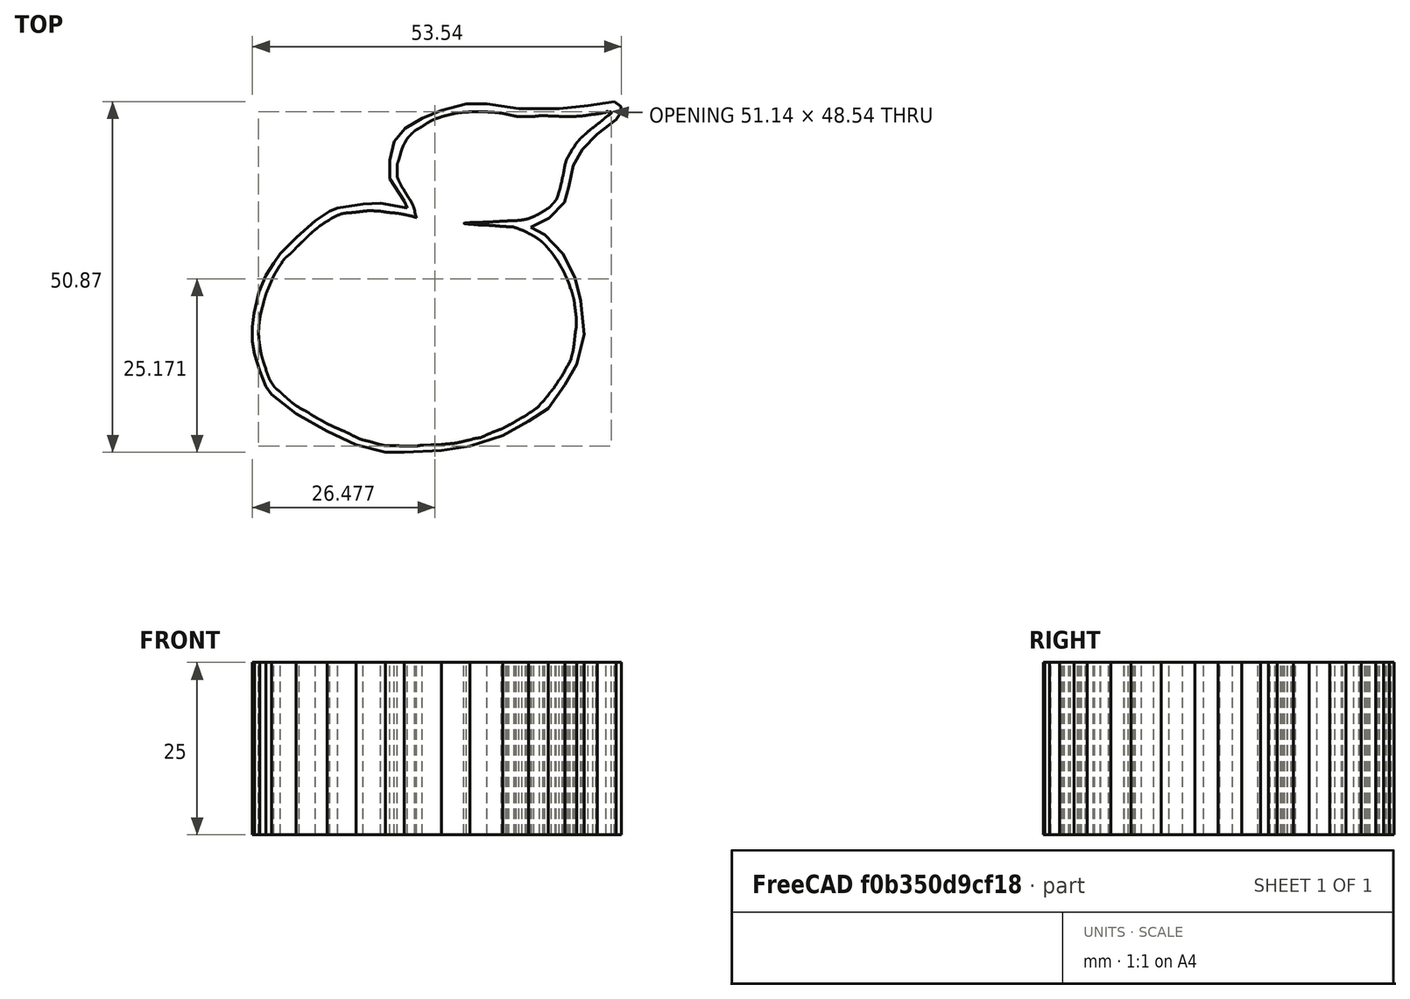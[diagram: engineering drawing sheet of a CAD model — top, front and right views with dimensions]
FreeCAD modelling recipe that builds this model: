
FCSTD DOCUMENT  (FreeCAD 0.18.3R)
Label: apple2
License: All rights reserved
LicenseURL: http://en.wikipedia.org/wiki/All_rights_reserved
objects: Part::Part2DObjectPython×3, Sketcher::SketchObject×2, Part::Extrusion×2, Part::Cut×1
note: 8 computed .brp shape members not serialized (recipe doc carries the construction recipe); baked Part::Feature solids carry a one-line shape summary decoded from their .brp

FEATURE [Sketcher::SketchObject] Sketch1180
  sketch-geometry (1180):
    g0: ArcOfCircle CenterX=919.407 CenterY=1602.46 CenterZ=0 NormalX=0 NormalY=0 NormalZ=1 AngleXU=-3.14159 Radius=144.686 StartAngle=1.63984 EndAngle=1.65794
    g1: ArcOfCircle CenterX=768.629 CenterY=1404.83 CenterZ=0 NormalX=0 NormalY=0 NormalZ=1 AngleXU=-3.14159 Radius=0.829803 StartAngle=1.5708 EndAngle=2.04218
    g2: ArcOfCircle CenterX=851.715 CenterY=737.772 CenterZ=0 NormalX=0 NormalY=0 NormalZ=1 AngleXU=0 Radius=243.363 StartAngle=4.83011 EndAngle=4.84867
    g3: ArcOfCircle CenterX=879.744 CenterY=533.379 CenterZ=0 NormalX=0 NormalY=0 NormalZ=1 AngleXU=0 Radius=37.0576 StartAngle=4.84867 EndAngle=4.92323
    g4: ArcOfCircle CenterX=1330.58 CenterY=-1573.07 CenterZ=0 NormalX=0 NormalY=0 NormalZ=1 AngleXU=-3.14159 Radius=2117.1 StartAngle=4.9221 EndAngle=4.92323
    g5: ArcOfCircle CenterX=1556.93 CenterY=-2624.68 CenterZ=0 NormalX=0 NormalY=0 NormalZ=1 AngleXU=-3.14159 Radius=3192.79 StartAngle=4.9201 EndAngle=4.92096
    g6: ArcOfCircle CenterX=2022.48 CenterY=-4824.32 CenterZ=0 NormalX=0 NormalY=0 NormalZ=1 AngleXU=-3.14159 Radius=5441.15 StartAngle=4.92096 EndAngle=4.92153
    g7: ArcOfCircle CenterX=874.349 CenterY=614.069 CenterZ=0 NormalX=0 NormalY=0 NormalZ=1 AngleXU=0 Radius=117.109 StartAngle=4.9201 EndAngle=4.944
    g8: ArcOfCircle CenterX=845.401 CenterY=736.81 CenterZ=0 NormalX=0 NormalY=0 NormalZ=1 AngleXU=0 Radius=243.218 StartAngle=4.944 EndAngle=4.95783
    g9: ArcOfCircle CenterX=845.173 CenterY=737.72 CenterZ=0 NormalX=0 NormalY=0 NormalZ=1 AngleXU=0 Radius=244.155 StartAngle=4.95783 EndAngle=4.97166
    g10: ArcOfCircle CenterX=1979.85 CenterY=-4623.55 CenterZ=0 NormalX=0 NormalY=0 NormalZ=1 AngleXU=-3.14159 Radius=5235.91 StartAngle=4.92153 EndAngle=4.9221
    g11: ArcOfCircle CenterX=876.443 CenterY=619.827 CenterZ=0 NormalX=0 NormalY=0 NormalZ=1 AngleXU=0 Radius=122.186 StartAngle=4.97166 EndAngle=4.99486
    g12: ArcOfCircle CenterX=928.112 CenterY=441.8 CenterZ=0 NormalX=0 NormalY=0 NormalZ=1 AngleXU=-3.14159 Radius=63.1874 StartAngle=4.95011 EndAngle=4.99486
    g13: ArcOfCircle CenterX=942.49 CenterY=382.464 CenterZ=0 NormalX=0 NormalY=0 NormalZ=1 AngleXU=-3.14159 Radius=124.24 StartAngle=4.92313 EndAngle=4.95011
    g14: ArcOfCircle CenterX=942.314 CenterY=383.285 CenterZ=0 NormalX=0 NormalY=0 NormalZ=1 AngleXU=-3.14159 Radius=123.4 StartAngle=4.89612 EndAngle=4.92313
    g15: ArcOfCircle CenterX=-1401.43 CenterY=-23166.9 CenterZ=0 NormalX=0 NormalY=0 NormalZ=1 AngleXU=0 Radius=24413 StartAngle=1.472 EndAngle=1.47223
    g16: ArcOfCircle CenterX=959.527 CenterY=1204.98 CenterZ=0 NormalX=0 NormalY=0 NormalZ=1 AngleXU=-3.14159 Radius=75.4491 StartAngle=1.45086 EndAngle=1.50424
    g17: ArcOfCircle CenterX=835.893 CenterY=1420.5 CenterZ=0 NormalX=0 NormalY=0 NormalZ=1 AngleXU=0 Radius=19.2721 StartAngle=1.8395 EndAngle=1.92574
    g18: ArcOfCircle CenterX=817.137 CenterY=1499.08 CenterZ=0 NormalX=0 NormalY=0 NormalZ=1 AngleXU=-3.14159 Radius=61.6309 StartAngle=1.89221 EndAngle=1.9355
    g19: ArcOfCircle CenterX=818.555 CenterY=1494.83 CenterZ=0 NormalX=0 NormalY=0 NormalZ=1 AngleXU=-3.14159 Radius=57.1444 StartAngle=1.84833 EndAngle=1.89221
    g20: ArcOfCircle CenterX=829.435 CenterY=1434.63 CenterZ=0 NormalX=0 NormalY=0 NormalZ=1 AngleXU=0 Radius=3.72542 StartAngle=2.01413 EndAngle=2.28314
    g21: ArcOfCircle CenterX=-7440.76 CenterY=-3669.64 CenterZ=0 NormalX=0 NormalY=0 NormalZ=1 AngleXU=-3.14159 Radius=9532.58 StartAngle=3.67931 EndAngle=3.67962
    g22: ArcOfCircle CenterX=768.629 CenterY=1402.13 CenterZ=0 NormalX=0 NormalY=0 NormalZ=1 AngleXU=0 Radius=1.86919 StartAngle=1.5708 EndAngle=2.30518
    g23: ArcOfCircle CenterX=1058.34 CenterY=669.531 CenterZ=0 NormalX=0 NormalY=0 NormalZ=1 AngleXU=0 Radius=803.247 StartAngle=1.81901 EndAngle=1.83669
    g24: ArcOfCircle CenterX=902.501 CenterY=1384.26 CenterZ=0 NormalX=0 NormalY=0 NormalZ=1 AngleXU=0 Radius=71.5381 StartAngle=1.69996 EndAngle=1.76066
    g25: ArcOfCircle CenterX=1318.79 CenterY=1567.21 CenterZ=0 NormalX=0 NormalY=0 NormalZ=1 AngleXU=0 Radius=673.017 StartAngle=3.67003 EndAngle=3.67544
    g26: ArcOfCircle CenterX=818.017 CenterY=3068.57 CenterZ=0 NormalX=0 NormalY=0 NormalZ=1 AngleXU=-3.14159 Radius=1614.3 StartAngle=1.63675 EndAngle=1.63984
    g27: ArcOfCircle CenterX=960.92 CenterY=1080.29 CenterZ=0 NormalX=0 NormalY=0 NormalZ=1 AngleXU=0 Radius=381.072 StartAngle=1.76067 EndAngle=1.79575
    g28: ArcOfCircle CenterX=786.319 CenterY=1347.74 CenterZ=0 NormalX=0 NormalY=0 NormalZ=1 AngleXU=0 Radius=52.1702 StartAngle=2.6013 EndAngle=2.67939
    g29: ArcOfCircle CenterX=2179.89 CenterY=0.0273162 CenterZ=0 NormalX=0 NormalY=0 NormalZ=1 AngleXU=0 Radius=1991.54 StartAngle=2.36577 EndAngle=2.37248
    g30: ArcOfCircle CenterX=857.853 CenterY=1405.69 CenterZ=0 NormalX=0 NormalY=0 NormalZ=1 AngleXU=0 Radius=40.2748 StartAngle=1.83669 EndAngle=1.99252
    g31: ArcOfCircle CenterX=791.991 CenterY=1412.51 CenterZ=0 NormalX=0 NormalY=0 NormalZ=1 AngleXU=0 Radius=4.93289 StartAngle=2.04902 EndAngle=2.19191
    g32: ArcOfCircle CenterX=923.045 CenterY=1227.68 CenterZ=0 NormalX=0 NormalY=0 NormalZ=1 AngleXU=0 Radius=231.243 StartAngle=2.07905 EndAngle=2.11989
    g33: ArcOfCircle CenterX=790.165 CenterY=1416.03 CenterZ=0 NormalX=0 NormalY=0 NormalZ=1 AngleXU=0 Radius=0.966328 StartAngle=1.5708 EndAngle=2.04902
    g34: ArcOfCircle CenterX=849.435 CenterY=1309.77 CenterZ=0 NormalX=0 NormalY=0 NormalZ=1 AngleXU=0 Radius=125.829 StartAngle=2.52191 EndAngle=2.56028
    g35: ArcOfCircle CenterX=790.165 CenterY=1418.14 CenterZ=0 NormalX=0 NormalY=0 NormalZ=1 AngleXU=-3.14159 Radius=1.13895 StartAngle=1.5708 EndAngle=2.10185
    g36: ArcOfCircle CenterX=790.392 CenterY=1278.24 CenterZ=0 NormalX=0 NormalY=0 NormalZ=1 AngleXU=0 Radius=74.222 StartAngle=3.20651 EndAngle=3.26556
    g37: ArcOfCircle CenterX=-7666.65 CenterY=-3804.43 CenterZ=0 NormalX=0 NormalY=0 NormalZ=1 AngleXU=-3.14159 Radius=9795.63 StartAngle=3.67962 EndAngle=3.67998
    g38: ArcOfCircle CenterX=826.334 CenterY=1314.34 CenterZ=0 NormalX=0 NormalY=0 NormalZ=1 AngleXU=0 Radius=106.8 StartAngle=2.02372 EndAngle=2.05292
    g39: ArcOfCircle CenterX=729.391 CenterY=1270.64 CenterZ=0 NormalX=0 NormalY=0 NormalZ=1 AngleXU=0 Radius=12.7493 StartAngle=3.26556 EndAngle=3.48294
    g40: ArcOfCircle CenterX=758.719 CenterY=1471.68 CenterZ=0 NormalX=0 NormalY=0 NormalZ=1 AngleXU=-3.14159 Radius=63.2306 StartAngle=2.10185 EndAngle=2.13158
    g41: ArcOfCircle CenterX=845.323 CenterY=1281.82 CenterZ=0 NormalX=0 NormalY=0 NormalZ=1 AngleXU=0 Radius=129.27 StartAngle=3.16027 EndAngle=3.20651
    g42: ArcOfCircle CenterX=1491.75 CenterY=1626.11 CenterZ=0 NormalX=0 NormalY=0 NormalZ=1 AngleXU=0 Radius=854.254 StartAngle=3.59782 EndAngle=3.61137
    g43: ArcOfCircle CenterX=1175.24 CenterY=1470.78 CenterZ=0 NormalX=0 NormalY=0 NormalZ=1 AngleXU=0 Radius=501.69 StartAngle=3.5752 EndAngle=3.59782
    g44: ArcOfCircle CenterX=785.625 CenterY=1259.2 CenterZ=0 NormalX=0 NormalY=0 NormalZ=1 AngleXU=0 Radius=57.2786 StartAngle=3.6364 EndAngle=3.66505
    g45: ArcOfCircle CenterX=746.533 CenterY=1478.31 CenterZ=0 NormalX=0 NormalY=0 NormalZ=1 AngleXU=-3.14159 Radius=75.56 StartAngle=2.02372 EndAngle=2.06479
    g46: ArcOfCircle CenterX=490.211 CenterY=1496.45 CenterZ=0 NormalX=0 NormalY=0 NormalZ=1 AngleXU=-3.14159 Radius=279.168 StartAngle=2.64115 EndAngle=2.64999
    g47: ArcOfCircle CenterX=753.834 CenterY=1464.76 CenterZ=0 NormalX=0 NormalY=0 NormalZ=1 AngleXU=-3.14159 Radius=60.1638 StartAngle=2.06479 EndAngle=2.11351
    g48: ArcOfCircle CenterX=847.491 CenterY=1311.04 CenterZ=0 NormalX=0 NormalY=0 NormalZ=1 AngleXU=0 Radius=123.503 StartAngle=2.56029 EndAngle=2.6013
    g49: ArcOfCircle CenterX=394.968 CenterY=1424.23 CenterZ=0 NormalX=0 NormalY=0 NormalZ=1 AngleXU=-3.14159 Radius=342.253 StartAngle=2.85482 EndAngle=2.86963
    g50: ArcOfCircle CenterX=787.781 CenterY=1291.39 CenterZ=0 NormalX=0 NormalY=0 NormalZ=1 AngleXU=0 Radius=74.7144 StartAngle=3.48294 EndAngle=3.5752
    g51: ArcOfCircle CenterX=814.71 CenterY=1336.09 CenterZ=0 NormalX=0 NormalY=0 NormalZ=1 AngleXU=0 Radius=82.1386 StartAngle=2.08653 EndAngle=2.11719
    g52: ArcOfCircle CenterX=756.113 CenterY=1460.98 CenterZ=0 NormalX=0 NormalY=0 NormalZ=1 AngleXU=-3.14159 Radius=55.7495 StartAngle=2.11351 EndAngle=2.15768
    g53: ArcOfCircle CenterX=945.228 CenterY=1187.86 CenterZ=0 NormalX=0 NormalY=0 NormalZ=1 AngleXU=0 Radius=276.826 StartAngle=2.04638 EndAngle=2.07905
    g54: LineSegment StartX=719.98 StartY=1316.94 StartZ=0 EndX=716 EndY=1304.86 EndZ=0
    g55: ArcOfCircle CenterX=1275.84 CenterY=1542.14 CenterZ=0 NormalX=0 NormalY=0 NormalZ=1 AngleXU=0 Radius=623.287 StartAngle=3.66505 EndAngle=3.67003
    g56: ArcOfCircle CenterX=884.535 CenterY=1273.75 CenterZ=0 NormalX=0 NormalY=0 NormalZ=1 AngleXU=0 Radius=174.829 StartAngle=2.30518 EndAngle=2.33402
    g57: ArcOfCircle CenterX=748.085 CenterY=1486.13 CenterZ=0 NormalX=0 NormalY=0 NormalZ=1 AngleXU=-3.14159 Radius=81.1549 StartAngle=2.17574 EndAngle=2.20706
    g58: ArcOfCircle CenterX=706.781 CenterY=1215.33 CenterZ=0 NormalX=0 NormalY=0 NormalZ=1 AngleXU=-3.14159 Radius=32.9861 StartAngle=3.71073 EndAngle=3.75642
    g59: ArcOfCircle CenterX=357.829 CenterY=1435.18 CenterZ=0 NormalX=0 NormalY=0 NormalZ=1 AngleXU=-3.14159 Radius=380.974 StartAngle=2.84009 EndAngle=2.85482
    g60: ArcOfCircle CenterX=765.534 CenterY=1410.9 CenterZ=0 NormalX=0 NormalY=0 NormalZ=1 AngleXU=-3.14159 Radius=7.64444 StartAngle=2.04218 EndAngle=2.13431
    g61: ArcOfCircle CenterX=764.784 CenterY=1412.09 CenterZ=0 NormalX=0 NormalY=0 NormalZ=1 AngleXU=-3.14159 Radius=9.04854 StartAngle=2.13431 EndAngle=2.22753
    g62: ArcOfCircle CenterX=648.737 CenterY=1353.46 CenterZ=0 NormalX=0 NormalY=0 NormalZ=1 AngleXU=-3.14159 Radius=78.8009 StartAngle=2.86963 EndAngle=2.91371
    g63: ArcOfCircle CenterX=720.624 CenterY=1226.06 CenterZ=0 NormalX=0 NormalY=0 NormalZ=1 AngleXU=-3.14159 Radius=15.4663 StartAngle=3.80221 EndAngle=3.88226
    g64: ArcOfCircle CenterX=826.535 CenterY=1418.33 CenterZ=0 NormalX=0 NormalY=0 NormalZ=1 AngleXU=0 Radius=17.5895 StartAngle=1.80228 EndAngle=2.04638
    g65: ArcOfCircle CenterX=416.988 CenterY=1416.79 CenterZ=0 NormalX=0 NormalY=0 NormalZ=1 AngleXU=-3.14159 Radius=319.02 StartAngle=2.82326 EndAngle=2.84009
    g66: LineSegment StartX=716 StartY=1304.86 StartZ=0 EndX=716 EndY=1287.56 EndZ=0
    g67: ArcOfCircle CenterX=632.711 CenterY=1424.26 CenterZ=0 NormalX=0 NormalY=0 NormalZ=1 AngleXU=-3.14159 Radius=119.445 StartAngle=2.6635 EndAngle=2.67939
    g68: ArcOfCircle CenterX=763.283 CenterY=1371.23 CenterZ=0 NormalX=0 NormalY=0 NormalZ=1 AngleXU=0 Radius=19.9993 StartAngle=2.37248 EndAngle=2.52191
    g69: ArcOfCircle CenterX=784.642 CenterY=1418.08 CenterZ=0 NormalX=0 NormalY=0 NormalZ=1 AngleXU=-3.14159 Radius=4.23293 StartAngle=2.15768 EndAngle=2.44887
    g70: ArcOfCircle CenterX=831.516 CenterY=1311.07 CenterZ=0 NormalX=0 NormalY=0 NormalZ=1 AngleXU=0 Radius=108.829 StartAngle=2.84728 EndAngle=2.91371
    g71: ArcOfCircle CenterX=720.065 CenterY=1223.83 CenterZ=0 NormalX=0 NormalY=0 NormalZ=1 AngleXU=-3.14159 Radius=17.2153 StartAngle=3.63639 EndAngle=3.71073
    g72: ArcOfCircle CenterX=817.882 CenterY=1330.49 CenterZ=0 NormalX=0 NormalY=0 NormalZ=1 AngleXU=0 Radius=88.57 StartAngle=2.05293 EndAngle=2.08652
    g73: ArcOfCircle CenterX=793.243 CenterY=1410.94 CenterZ=0 NormalX=0 NormalY=0 NormalZ=1 AngleXU=0 Radius=6.94498 StartAngle=2.3262 EndAngle=2.44887
    g74: ArcOfCircle CenterX=741.67 CenterY=1245.31 CenterZ=0 NormalX=0 NormalY=0 NormalZ=1 AngleXU=0 Radius=13.0499 StartAngle=3.61137 EndAngle=3.88226
    g75: ArcOfCircle CenterX=707.064 CenterY=1215.53 CenterZ=0 NormalX=0 NormalY=0 NormalZ=1 AngleXU=-3.14159 Radius=32.6394 StartAngle=3.75641 EndAngle=3.8022
    g76: ArcOfCircle CenterX=818.993 CenterY=1449.96 CenterZ=0 NormalX=0 NormalY=0 NormalZ=1 AngleXU=-3.14159 Radius=14.9207 StartAngle=1.98949 EndAngle=2.07606
    g77: ArcOfCircle CenterX=763.401 CenterY=1413.88 CenterZ=0 NormalX=0 NormalY=0 NormalZ=1 AngleXU=-3.14159 Radius=11.3144 StartAngle=2.22753 EndAngle=2.30636
    g78: ArcOfCircle CenterX=785.154 CenterY=1335.15 CenterZ=0 NormalX=0 NormalY=0 NormalZ=1 AngleXU=0 Radius=56.9989 StartAngle=2.64115 EndAngle=2.7451
    g79: ArcOfCircle CenterX=381.455 CenterY=1554.68 CenterZ=0 NormalX=0 NormalY=0 NormalZ=1 AngleXU=-3.14159 Radius=402.533 StartAngle=2.64999 EndAngle=2.65671
    g80: ArcOfCircle CenterX=1152.7 CenterY=1287.56 CenterZ=0 NormalX=0 NormalY=0 NormalZ=1 AngleXU=0 Radius=436.695 StartAngle=3.14159 EndAngle=3.16027
    g81: ArcOfCircle CenterX=765.072 CenterY=1461.56 CenterZ=0 NormalX=0 NormalY=0 NormalZ=1 AngleXU=-3.14159 Radius=51.287 StartAngle=2.13158 EndAngle=2.17574
    g82: ArcOfCircle CenterX=877.006 CenterY=1297.28 CenterZ=0 NormalX=0 NormalY=0 NormalZ=1 AngleXU=0 Radius=156.362 StartAngle=2.79665 EndAngle=2.84728
    g83: ArcOfCircle CenterX=231.475 CenterY=905.528 CenterZ=0 NormalX=0 NormalY=0 NormalZ=1 AngleXU=-3.14159 Radius=599.756 StartAngle=3.67696 EndAngle=3.67931
    g84: ArcOfCircle CenterX=792.702 CenterY=1411.52 CenterZ=0 NormalX=0 NormalY=0 NormalZ=1 AngleXU=0 Radius=6.15492 StartAngle=2.19191 EndAngle=2.3262
    g85: ArcOfCircle CenterX=775.589 CenterY=1400.42 CenterZ=0 NormalX=0 NormalY=0 NormalZ=1 AngleXU=0 Radius=6.84968 StartAngle=2.11719 EndAngle=2.30636
    g86: ArcOfCircle CenterX=867.091 CenterY=1300.85 CenterZ=0 NormalX=0 NormalY=0 NormalZ=1 AngleXU=0 Radius=145.827 StartAngle=2.7451 EndAngle=2.79665
    g87: ArcOfCircle CenterX=772.459 CenterY=1226.42 CenterZ=0 NormalX=0 NormalY=0 NormalZ=1 AngleXU=0 Radius=29.2364 StartAngle=3.67696 EndAngle=3.7198
    g88: ArcOfCircle CenterX=835.53 CenterY=1421.82 CenterZ=0 NormalX=0 NormalY=0 NormalZ=1 AngleXU=0 Radius=17.9038 StartAngle=1.74836 EndAngle=1.8395
    g89: ArcOfCircle CenterX=904.424 CenterY=1312.54 CenterZ=0 NormalX=0 NormalY=0 NormalZ=1 AngleXU=0 Radius=186.816 StartAngle=3.7198 EndAngle=3.73068
    g90: ArcOfCircle CenterX=809.835 CenterY=3192.41 CenterZ=0 NormalX=0 NormalY=0 NormalZ=1 AngleXU=-3.14159 Radius=1738.4 StartAngle=1.63339 EndAngle=1.63676
    g91: ArcOfCircle CenterX=932.6 CenterY=1147.45 CenterZ=0 NormalX=0 NormalY=0 NormalZ=1 AngleXU=0 Radius=310.256 StartAngle=1.6562 EndAngle=1.67798
    g92: ArcOfCircle CenterX=927.225 CenterY=1210.23 CenterZ=0 NormalX=0 NormalY=0 NormalZ=1 AngleXU=0 Radius=247.251 StartAngle=1.63039 EndAngle=1.6562
    g93: ArcOfCircle CenterX=923.157 CenterY=1325.06 CenterZ=0 NormalX=0 NormalY=0 NormalZ=1 AngleXU=0 Radius=209.348 StartAngle=3.73068 EndAngle=3.74177
    g94: ArcOfCircle CenterX=846.043 CenterY=1353.53 CenterZ=0 NormalX=0 NormalY=0 NormalZ=1 AngleXU=0 Radius=83.7041 StartAngle=2.11989 EndAngle=2.20705
    g95: ArcOfCircle CenterX=1410.52 CenterY=1621.43 CenterZ=0 NormalX=0 NormalY=0 NormalZ=1 AngleXU=0 Radius=779.574 StartAngle=3.67544 EndAngle=3.68028
    g96: ArcOfCircle CenterX=638.353 CenterY=1133.6 CenterZ=0 NormalX=0 NormalY=0 NormalZ=1 AngleXU=-3.14159 Radius=134.188 StartAngle=3.53735 EndAngle=3.62538
    g97: ArcOfCircle CenterX=920.69 CenterY=1323.37 CenterZ=0 NormalX=0 NormalY=0 NormalZ=1 AngleXU=0 Radius=206.358 StartAngle=3.74177 EndAngle=3.75298
    g98: ArcOfCircle CenterX=684.77 CenterY=1157.99 CenterZ=0 NormalX=0 NormalY=0 NormalZ=1 AngleXU=-3.14159 Radius=81.7539 StartAngle=3.62538 EndAngle=3.75298
    g99: ArcOfCircle CenterX=1023.04 CenterY=808.811 CenterZ=0 NormalX=0 NormalY=0 NormalZ=1 AngleXU=0 Radius=659.564 StartAngle=1.79575 EndAngle=1.81901
    g100: ArcOfCircle CenterX=930.36 CenterY=1225.85 CenterZ=0 NormalX=0 NormalY=0 NormalZ=1 AngleXU=0 Radius=241.122 StartAngle=2.33402 EndAngle=2.36577
    g101: ArcOfCircle CenterX=527.147 CenterY=1081.42 CenterZ=0 NormalX=0 NormalY=0 NormalZ=1 AngleXU=0 Radius=57.8297 StartAngle=2.2214 EndAngle=2.2808
    g102: ArcOfCircle CenterX=819.57 CenterY=1447.88 CenterZ=0 NormalX=0 NormalY=0 NormalZ=1 AngleXU=-3.14159 Radius=12.7698 StartAngle=1.80228 EndAngle=1.90496
    g103: ArcOfCircle CenterX=744.818 CenterY=1168.33 CenterZ=0 NormalX=0 NormalY=0 NormalZ=1 AngleXU=-3.14159 Radius=22.1823 StartAngle=3.14159 EndAngle=3.45253
    g104: ArcOfCircle CenterX=643.698 CenterY=1135.83 CenterZ=0 NormalX=0 NormalY=0 NormalZ=1 AngleXU=-3.14159 Radius=128.395 StartAngle=3.45253 EndAngle=3.53735
    g105: ArcOfCircle CenterX=407.079 CenterY=1541.18 CenterZ=0 NormalX=0 NormalY=0 NormalZ=1 AngleXU=-3.14159 Radius=373.57 StartAngle=2.65671 EndAngle=2.6635
    g106: ArcOfCircle CenterX=929.419 CenterY=1177.02 CenterZ=0 NormalX=0 NormalY=0 NormalZ=1 AngleXU=0 Radius=280.516 StartAngle=1.67798 EndAngle=1.69996
    g107: ArcOfCircle CenterX=791.717 CenterY=3481.48 CenterZ=0 NormalX=0 NormalY=0 NormalZ=1 AngleXU=-3.14159 Radius=2028.05 StartAngle=1.63039 EndAngle=1.63339
    g108: ArcOfCircle CenterX=829.023 CenterY=1458.08 CenterZ=0 NormalX=0 NormalY=0 NormalZ=1 AngleXU=-3.14159 Radius=18.9368 StartAngle=1.74836 EndAngle=1.84833
    g109: ArcOfCircle CenterX=818.33 CenterY=1451.45 CenterZ=0 NormalX=0 NormalY=0 NormalZ=1 AngleXU=-3.14159 Radius=16.5511 StartAngle=1.90496 EndAngle=1.9895
    g110: ArcOfCircle CenterX=823.892 CenterY=1481.39 CenterZ=0 NormalX=0 NormalY=0 NormalZ=1 AngleXU=-3.14159 Radius=42.6938 StartAngle=1.9355 EndAngle=1.99252
    g111: ArcOfCircle CenterX=834.995 CenterY=1422.92 CenterZ=0 NormalX=0 NormalY=0 NormalZ=1 AngleXU=0 Radius=16.6868 StartAngle=1.92574 EndAngle=2.01413
    g112: ArcOfCircle CenterX=823.975 CenterY=1440.95 CenterZ=0 NormalX=0 NormalY=0 NormalZ=1 AngleXU=-3.14159 Radius=4.62783 StartAngle=2.07606 EndAngle=2.28314
    g113: ArcOfCircle CenterX=-9815.61 CenterY=-5087.87 CenterZ=0 NormalX=0 NormalY=0 NormalZ=1 AngleXU=-3.14159 Radius=12298.7 StartAngle=3.67998 EndAngle=3.68028
    g114: ArcOfCircle CenterX=773.371 CenterY=1168.33 CenterZ=0 NormalX=0 NormalY=0 NormalZ=1 AngleXU=0 Radius=6.37126 StartAngle=3.14159 EndAngle=3.34669
    g115: ArcOfCircle CenterX=840.588 CenterY=1182.31 CenterZ=0 NormalX=0 NormalY=0 NormalZ=1 AngleXU=0 Radius=75.027 StartAngle=3.34669 EndAngle=3.38037
    g116: ArcOfCircle CenterX=846.631 CenterY=1183.78 CenterZ=0 NormalX=0 NormalY=0 NormalZ=1 AngleXU=0 Radius=81.2468 StartAngle=3.38037 EndAngle=3.41711
    g117: ArcOfCircle CenterX=862.611 CenterY=1188.3 CenterZ=0 NormalX=0 NormalY=0 NormalZ=1 AngleXU=0 Radius=97.8526 StartAngle=3.41712 EndAngle=3.44908
    g118: ArcOfCircle CenterX=775.46 CenterY=1185.71 CenterZ=0 NormalX=0 NormalY=0 NormalZ=1 AngleXU=-3.14159 Radius=34.3209 StartAngle=1.243 EndAngle=1.2902
    g119: LineSegment StartX=769.348 StartY=1158.68 StartZ=0 EndX=771.696 EndY=1151.29 EndZ=0
    g120: LineSegment StartX=771.696 StartY=1151.29 StartZ=0 EndX=767.598 EndY=1152.29 EndZ=0
    g121: ArcOfCircle CenterX=777.462 CenterY=1192.65 CenterZ=0 NormalX=0 NormalY=0 NormalZ=1 AngleXU=-3.14159 Radius=41.549 StartAngle=1.2902 EndAngle=1.33111
    g122: ArcOfCircle CenterX=774.495 CenterY=1182.87 CenterZ=0 NormalX=0 NormalY=0 NormalZ=1 AngleXU=-3.14159 Radius=31.3243 StartAngle=1.19931 EndAngle=1.243
    g123: ArcOfCircle CenterX=724.989 CenterY=1020.68 CenterZ=0 NormalX=0 NormalY=0 NormalZ=1 AngleXU=0 Radius=138.718 StartAngle=1.34062 EndAngle=1.36379
    g124: ArcOfCircle CenterX=764.119 CenterY=1156.24 CenterZ=0 NormalX=0 NormalY=0 NormalZ=1 AngleXU=-3.14159 Radius=2.74141 StartAngle=0.938831 EndAngle=1.19931
    g125: ArcOfCircle CenterX=761.112 CenterY=1152.13 CenterZ=0 NormalX=0 NormalY=0 NormalZ=1 AngleXU=0 Radius=2.35016 StartAngle=0.938829 EndAngle=1.2871
    g126: ArcOfCircle CenterX=730.794 CenterY=1048.14 CenterZ=0 NormalX=0 NormalY=0 NormalZ=1 AngleXU=0 Radius=110.664 StartAngle=1.2871 EndAngle=1.30892
    g127: ArcOfCircle CenterX=735.81 CenterY=1066.86 CenterZ=0 NormalX=0 NormalY=0 NormalZ=1 AngleXU=0 Radius=91.2877 StartAngle=1.30892 EndAngle=1.34062
    g128: ArcOfCircle CenterX=1258.21 CenterY=3559.6 CenterZ=0 NormalX=0 NormalY=0 NormalZ=1 AngleXU=-3.14159 Radius=2455.59 StartAngle=1.36224 EndAngle=1.36379
    g129: ArcOfCircle CenterX=1409.85 CenterY=4296.35 CenterZ=0 NormalX=0 NormalY=0 NormalZ=1 AngleXU=-3.14159 Radius=3207.77 StartAngle=1.35931 EndAngle=1.36059
    g130: ArcOfCircle CenterX=1951.85 CenterY=6836.7 CenterZ=0 NormalX=0 NormalY=0 NormalZ=1 AngleXU=-3.14159 Radius=5805.3 StartAngle=1.36059 EndAngle=1.36142
    g131: ArcOfCircle CenterX=697.048 CenterY=1005 CenterZ=0 NormalX=0 NormalY=0 NormalZ=1 AngleXU=0 Radius=159.809 StartAngle=1.38278 EndAngle=1.43076
    g132: ArcOfCircle CenterX=649.041 CenterY=752.686 CenterZ=0 NormalX=0 NormalY=0 NormalZ=1 AngleXU=0 Radius=416.647 StartAngle=1.35931 EndAngle=1.38277
    g133: ArcOfCircle CenterX=695.484 CenterY=993.902 CenterZ=0 NormalX=0 NormalY=0 NormalZ=1 AngleXU=0 Radius=171.014 StartAngle=1.43076 EndAngle=1.47678
    g134: ArcOfCircle CenterX=716.656 CenterY=1374.52 CenterZ=0 NormalX=0 NormalY=0 NormalZ=1 AngleXU=-3.14159 Radius=210.056 StartAngle=1.46688 EndAngle=1.49661
    g135: ArcOfCircle CenterX=661.879 CenterY=637.53 CenterZ=0 NormalX=0 NormalY=0 NormalZ=1 AngleXU=0 Radius=528.967 StartAngle=1.47678 EndAngle=1.49661
    g136: ArcOfCircle CenterX=725.851 CenterY=1462.68 CenterZ=0 NormalX=0 NormalY=0 NormalZ=1 AngleXU=-3.14159 Radius=298.696 StartAngle=1.44404 EndAngle=1.46688
    g137: ArcOfCircle CenterX=1921.49 CenterY=6693.78 CenterZ=0 NormalX=0 NormalY=0 NormalZ=1 AngleXU=-3.14159 Radius=5659.18 StartAngle=1.36142 EndAngle=1.36224
    g138: ArcOfCircle CenterX=723.02 CenterY=1440.47 CenterZ=0 NormalX=0 NormalY=0 NormalZ=1 AngleXU=-3.14159 Radius=276.305 StartAngle=1.42094 EndAngle=1.44404
    g139: ArcOfCircle CenterX=694.79 CenterY=1253.5 CenterZ=0 NormalX=0 NormalY=0 NormalZ=1 AngleXU=-3.14159 Radius=87.2141 StartAngle=1.36639 EndAngle=1.42094
    g140: ArcOfCircle CenterX=635.754 CenterY=793.019 CenterZ=0 NormalX=0 NormalY=0 NormalZ=1 AngleXU=0 Radius=377.885 StartAngle=1.49087 EndAngle=1.53397
    g141: ArcOfCircle CenterX=658.687 CenterY=1079.35 CenterZ=0 NormalX=0 NormalY=0 NormalZ=1 AngleXU=0 Radius=90.6385 StartAngle=1.36639 EndAngle=1.49087
    g142: ArcOfCircle CenterX=635.768 CenterY=793.401 CenterZ=0 NormalX=0 NormalY=0 NormalZ=1 AngleXU=0 Radius=377.502 StartAngle=1.53397 EndAngle=1.57717
    g143: ArcOfCircle CenterX=633.957 CenterY=1077.49 CenterZ=0 NormalX=0 NormalY=0 NormalZ=1 AngleXU=0 Radius=93.4092 StartAngle=1.57717 EndAngle=1.69915
    g144: ArcOfCircle CenterX=1415.88 CenterY=-4912.56 CenterZ=0 NormalX=0 NormalY=0 NormalZ=1 AngleXU=0 Radius=6134.28 StartAngle=1.70212 EndAngle=1.70304
    g145: ArcOfCircle CenterX=879.985 CenterY=-828.744 CenterZ=0 NormalX=0 NormalY=0 NormalZ=1 AngleXU=0 Radius=2015.45 StartAngle=1.69915 EndAngle=1.70119
    g146: ArcOfCircle CenterX=586.319 CenterY=996.639 CenterZ=0 NormalX=0 NormalY=0 NormalZ=1 AngleXU=0 Radius=168.731 StartAngle=1.63199 EndAngle=1.68737
    g147: ArcOfCircle CenterX=1132.47 CenterY=-2781.98 CenterZ=0 NormalX=0 NormalY=0 NormalZ=1 AngleXU=0 Radius=3984.93 StartAngle=1.70304 EndAngle=1.70431
    g148: ArcOfCircle CenterX=574.989 CenterY=1368.59 CenterZ=0 NormalX=0 NormalY=0 NormalZ=1 AngleXU=-3.14159 Radius=202.913 StartAngle=1.67732 EndAngle=1.70431
    g149: ArcOfCircle CenterX=540.419 CenterY=1691.89 CenterZ=0 NormalX=0 NormalY=0 NormalZ=1 AngleXU=-3.14159 Radius=528.053 StartAngle=1.6641 EndAngle=1.67732
    g150: ArcOfCircle CenterX=538.047 CenterY=1717.24 CenterZ=0 NormalX=0 NormalY=0 NormalZ=1 AngleXU=-3.14159 Radius=553.517 StartAngle=1.65099 EndAngle=1.6641
    g151: ArcOfCircle CenterX=555.383 CenterY=1501.55 CenterZ=0 NormalX=0 NormalY=0 NormalZ=1 AngleXU=-3.14159 Radius=337.127 StartAngle=1.63199 EndAngle=1.65099
    g152: ArcOfCircle CenterX=1365.4 CenterY=-4530.41 CenterZ=0 NormalX=0 NormalY=0 NormalZ=1 AngleXU=0 Radius=5748.81 StartAngle=1.70119 EndAngle=1.70212
    g153: ArcOfCircle CenterX=574.512 CenterY=1083.8 CenterZ=0 NormalX=0 NormalY=0 NormalZ=1 AngleXU=0 Radius=80.728 StartAngle=1.7692 EndAngle=1.85042
    g154: ArcOfCircle CenterX=578.346 CenterY=1064.73 CenterZ=0 NormalX=0 NormalY=0 NormalZ=1 AngleXU=0 Radius=100.18 StartAngle=1.68737 EndAngle=1.7692
    g155: ArcOfCircle CenterX=546.918 CenterY=1164.16 CenterZ=0 NormalX=0 NormalY=0 NormalZ=1 AngleXU=-3.14159 Radius=5.16696 StartAngle=1.72 EndAngle=1.85791
    g156: ArcOfCircle CenterX=554.065 CenterY=1155 CenterZ=0 NormalX=0 NormalY=0 NormalZ=1 AngleXU=0 Radius=6.64326 StartAngle=1.85042 EndAngle=2.35619
    g157: ArcOfCircle CenterX=548.42 CenterY=1160.65 CenterZ=0 NormalX=0 NormalY=0 NormalZ=1 AngleXU=-3.14159 Radius=1.33986 StartAngle=2.00311 EndAngle=2.35619
    g158: ArcOfCircle CenterX=547.13 CenterY=1163.44 CenterZ=0 NormalX=0 NormalY=0 NormalZ=1 AngleXU=-3.14159 Radius=4.41742 StartAngle=1.85791 EndAngle=2.00311
    g159: ArcOfCircle CenterX=546.995 CenterY=1163.65 CenterZ=0 NormalX=0 NormalY=0 NormalZ=1 AngleXU=-3.14159 Radius=4.65182 StartAngle=1.5708 EndAngle=1.72
    g160: ArcOfCircle CenterX=546.995 CenterY=1152.03 CenterZ=0 NormalX=0 NormalY=0 NormalZ=1 AngleXU=0 Radius=6.9693 StartAngle=1.5708 EndAngle=2.01484
    g161: ArcOfCircle CenterX=512.405 CenterY=1156.6 CenterZ=0 NormalX=0 NormalY=0 NormalZ=1 AngleXU=-3.14159 Radius=14.0844 StartAngle=2.25515 EndAngle=2.35619
    g162: ArcOfCircle CenterX=754.402 CenterY=716.05 CenterZ=0 NormalX=0 NormalY=0 NormalZ=1 AngleXU=0 Radius=489.77 StartAngle=2.01484 EndAngle=2.036
    g163: ArcOfCircle CenterX=532.316 CenterY=1136.68 CenterZ=0 NormalX=0 NormalY=0 NormalZ=1 AngleXU=0 Radius=14.0745 StartAngle=2.06329 EndAngle=2.35619
    g164: ArcOfCircle CenterX=503.561 CenterY=1167.44 CenterZ=0 NormalX=0 NormalY=0 NormalZ=1 AngleXU=-3.14159 Radius=28.0739 StartAngle=2.19484 EndAngle=2.25515
    g165: ArcOfCircle CenterX=503.551 CenterY=1167.45 CenterZ=0 NormalX=0 NormalY=0 NormalZ=1 AngleXU=-3.14159 Radius=28.0903 StartAngle=2.13454 EndAngle=2.19484
    g166: ArcOfCircle CenterX=595.249 CenterY=995.266 CenterZ=0 NormalX=0 NormalY=0 NormalZ=1 AngleXU=0 Radius=167.085 StartAngle=2.12568 EndAngle=2.16064
    g167: ArcOfCircle CenterX=510.993 CenterY=1155.68 CenterZ=0 NormalX=0 NormalY=0 NormalZ=1 AngleXU=-3.14159 Radius=14.1646 StartAngle=2.0339 EndAngle=2.13454
    g168: ArcOfCircle CenterX=560.506 CenterY=1056.52 CenterZ=0 NormalX=0 NormalY=0 NormalZ=1 AngleXU=0 Radius=96.6715 StartAngle=2.0339 EndAngle=2.08959
    g169: ArcOfCircle CenterX=701.923 CenterY=820.599 CenterZ=0 NormalX=0 NormalY=0 NormalZ=1 AngleXU=0 Radius=372.79 StartAngle=2.036 EndAngle=2.06328
    g170: ArcOfCircle CenterX=598.129 CenterY=990.62 CenterZ=0 NormalX=0 NormalY=0 NormalZ=1 AngleXU=0 Radius=172.552 StartAngle=2.08959 EndAngle=2.12568
    g171: ArcOfCircle CenterX=478.424 CenterY=1156.33 CenterZ=0 NormalX=0 NormalY=0 NormalZ=1 AngleXU=-3.14159 Radius=32.1655 StartAngle=2.22069 EndAngle=2.27362
    g172: ArcOfCircle CenterX=521.418 CenterY=1105.57 CenterZ=0 NormalX=0 NormalY=0 NormalZ=1 AngleXU=0 Radius=34.3492 StartAngle=2.16064 EndAngle=2.27362
    g173: ArcOfCircle CenterX=494.977 CenterY=1127.05 CenterZ=0 NormalX=0 NormalY=0 NormalZ=1 AngleXU=0 Radius=1.95308 StartAngle=1.5708 EndAngle=2.13569
    g174: ArcOfCircle CenterX=484.21 CenterY=1148.71 CenterZ=0 NormalX=0 NormalY=0 NormalZ=1 AngleXU=-3.14159 Radius=22.6041 StartAngle=2.15173 EndAngle=2.22069
    g175: ArcOfCircle CenterX=484.829 CenterY=1147.77 CenterZ=0 NormalX=0 NormalY=0 NormalZ=1 AngleXU=-3.14159 Radius=21.4753 StartAngle=2.09195 EndAngle=2.15173
    g176: ArcOfCircle CenterX=494.977 CenterY=1130.09 CenterZ=0 NormalX=0 NormalY=0 NormalZ=1 AngleXU=-3.14159 Radius=1.09419 StartAngle=1.5708 EndAngle=2.09195
    g177: ArcOfCircle CenterX=768.113 CenterY=801.079 CenterZ=0 NormalX=0 NormalY=0 NormalZ=1 AngleXU=0 Radius=427.501 StartAngle=2.2808 EndAngle=2.29439
    g178: ArcOfCircle CenterX=507.704 CenterY=1106.97 CenterZ=0 NormalX=0 NormalY=0 NormalZ=1 AngleXU=0 Radius=25.7275 StartAngle=2.13569 EndAngle=2.2214
    g179: ArcOfCircle CenterX=412.127 CenterY=1206.47 CenterZ=0 NormalX=0 NormalY=0 NormalZ=1 AngleXU=-3.14159 Radius=112.034 StartAngle=2.22911 EndAngle=2.25604
    g180: ArcOfCircle CenterX=438.797 CenterY=1173.84 CenterZ=0 NormalX=0 NormalY=0 NormalZ=1 AngleXU=-3.14159 Radius=69.893 StartAngle=2.25604 EndAngle=2.29439
    g181: ArcOfCircle CenterX=415.614 CenterY=1201.96 CenterZ=0 NormalX=0 NormalY=0 NormalZ=1 AngleXU=-3.14159 Radius=106.335 StartAngle=2.20193 EndAngle=2.22911
    g182: ArcOfCircle CenterX=454.767 CenterY=1148.39 CenterZ=0 NormalX=0 NormalY=0 NormalZ=1 AngleXU=-3.14159 Radius=39.9802 StartAngle=2.14551 EndAngle=2.20193
    g183: ArcOfCircle CenterX=-3030.24 CenterY=4633.41 CenterZ=0 NormalX=0 NormalY=0 NormalZ=1 AngleXU=-3.14159 Radius=4966.59 StartAngle=2.34129 EndAngle=2.34308
    g184: ArcOfCircle CenterX=486.98 CenterY=1098.65 CenterZ=0 NormalX=0 NormalY=0 NormalZ=1 AngleXU=0 Radius=19.2785 StartAngle=2.14551 EndAngle=2.30878
    g185: ArcOfCircle CenterX=923.813 CenterY=616.149 CenterZ=0 NormalX=0 NormalY=0 NormalZ=1 AngleXU=0 Radius=670.137 StartAngle=2.31994 EndAngle=2.33584
    g186: ArcOfCircle CenterX=1012.08 CenterY=521.242 CenterZ=0 NormalX=0 NormalY=0 NormalZ=1 AngleXU=0 Radius=799.745 StartAngle=2.30878 EndAngle=2.31994
    g187: ArcOfCircle CenterX=1143.79 CenterY=387.028 CenterZ=0 NormalX=0 NormalY=0 NormalZ=1 AngleXU=0 Radius=987.766 StartAngle=2.33584 EndAngle=2.34773
    g188: ArcOfCircle CenterX=-3709.17 CenterY=5322.84 CenterZ=0 NormalX=0 NormalY=0 NormalZ=1 AngleXU=-3.14159 Radius=5934.19 StartAngle=2.34575 EndAngle=2.34773
    g189: ArcOfCircle CenterX=-2333.42 CenterY=3918.06 CenterZ=0 NormalX=0 NormalY=0 NormalZ=1 AngleXU=-3.14159 Radius=3967.96 StartAngle=2.34308 EndAngle=2.34575
    g190: ArcOfCircle CenterX=-4832.66 CenterY=5578.88 CenterZ=0 NormalX=0 NormalY=0 NormalZ=1 AngleXU=-3.14159 Radius=6928.69 StartAngle=2.43036 EndAngle=2.43072
    g191: ArcOfCircle CenterX=1172.82 CenterY=1198.76 CenterZ=0 NormalX=0 NormalY=0 NormalZ=1 AngleXU=0 Radius=1.16785 StartAngle=5.60968 EndAngle=6.27654
    g192: ArcOfCircle CenterX=358.19 CenterY=1142.43 CenterZ=0 NormalX=0 NormalY=0 NormalZ=1 AngleXU=-3.14159 Radius=101.578 StartAngle=2.31194 EndAngle=2.34129
    g193: ArcOfCircle CenterX=457.012 CenterY=1034.45 CenterZ=0 NormalX=0 NormalY=0 NormalZ=1 AngleXU=0 Radius=44.7957 StartAngle=2.31194 EndAngle=2.35955
    g194: ArcOfCircle CenterX=524.183 CenterY=968 CenterZ=0 NormalX=0 NormalY=0 NormalZ=1 AngleXU=0 Radius=139.287 StartAngle=2.381 EndAngle=2.40223
    g195: ArcOfCircle CenterX=517.752 CenterY=974.12 CenterZ=0 NormalX=0 NormalY=0 NormalZ=1 AngleXU=0 Radius=130.409 StartAngle=2.35955 EndAngle=2.381
    g196: ArcOfCircle CenterX=489.6 CenterY=999.537 CenterZ=0 NormalX=0 NormalY=0 NormalZ=1 AngleXU=0 Radius=92.4829 StartAngle=2.40223 EndAngle=2.43108
    g197: ArcOfCircle CenterX=-4839.3 CenterY=5584.61 CenterZ=0 NormalX=0 NormalY=0 NormalZ=1 AngleXU=-3.14159 Radius=6937.46 StartAngle=2.43072 EndAngle=2.43108
    g198: ArcOfCircle CenterX=302.375 CenterY=1172.13 CenterZ=0 NormalX=0 NormalY=0 NormalZ=1 AngleXU=-3.14159 Radius=163.049 StartAngle=2.28391 EndAngle=2.30975
    g199: ArcOfCircle CenterX=-4264.7 CenterY=5089.49 CenterZ=0 NormalX=0 NormalY=0 NormalZ=1 AngleXU=-3.14159 Radius=6178.97 StartAngle=2.43 EndAngle=2.43036
    g200: ArcOfCircle CenterX=-276.812 CenterY=1650.71 CenterZ=0 NormalX=0 NormalY=0 NormalZ=1 AngleXU=-3.14159 Radius=913.187 StartAngle=2.42854 EndAngle=2.43
    g201: ArcOfCircle CenterX=398.342 CenterY=1066.81 CenterZ=0 NormalX=0 NormalY=0 NormalZ=1 AngleXU=-3.14159 Radius=20.5624 StartAngle=2.30975 EndAngle=2.42854
    g202: ArcOfCircle CenterX=385.507 CenterY=1021.4 CenterZ=0 NormalX=0 NormalY=0 NormalZ=1 AngleXU=0 Radius=3.50913 StartAngle=2.47897 EndAngle=3.13978
    g203: ArcOfCircle CenterX=175.049 CenterY=1319.33 CenterZ=0 NormalX=0 NormalY=0 NormalZ=1 AngleXU=-3.14159 Radius=357.678 StartAngle=2.26619 EndAngle=2.28391
    g204: ArcOfCircle CenterX=433.656 CenterY=992.887 CenterZ=0 NormalX=0 NormalY=0 NormalZ=1 AngleXU=0 Radius=58.6769 StartAngle=2.26173 EndAngle=2.36658
    g205: ArcOfCircle CenterX=500.552 CenterY=931.632 CenterZ=0 NormalX=0 NormalY=0 NormalZ=1 AngleXU=0 Radius=149.434 StartAngle=2.43459 EndAngle=2.47897
    g206: ArcOfCircle CenterX=466.451 CenterY=960.765 CenterZ=0 NormalX=0 NormalY=0 NormalZ=1 AngleXU=0 Radius=104.583 StartAngle=2.36658 EndAngle=2.43459
    g207: ArcOfCircle CenterX=380.851 CenterY=1021.41 CenterZ=0 NormalX=0 NormalY=0 NormalZ=1 AngleXU=-3.14159 Radius=1.14744 StartAngle=2.61335 EndAngle=3.13978
    g208: ArcOfCircle CenterX=318.607 CenterY=1057.73 CenterZ=0 NormalX=0 NormalY=0 NormalZ=1 AngleXU=-3.14159 Radius=73.214 StartAngle=2.58655 EndAngle=2.61335
    g209: ArcOfCircle CenterX=-1081 CenterY=2824.58 CenterZ=0 NormalX=0 NormalY=0 NormalZ=1 AngleXU=-3.14159 Radius=2318.14 StartAngle=2.26173 EndAngle=2.26619
    g210: ArcOfCircle CenterX=304.119 CenterY=1068.38 CenterZ=0 NormalX=0 NormalY=0 NormalZ=1 AngleXU=-3.14159 Radius=91.1659 StartAngle=2.51608 EndAngle=2.54519
    g211: ArcOfCircle CenterX=332.368 CenterY=1049.2 CenterZ=0 NormalX=0 NormalY=0 NormalZ=1 AngleXU=-3.14159 Radius=57.0225 StartAngle=2.54519 EndAngle=2.58655
    g212: ArcOfCircle CenterX=490.104 CenterY=934.049 CenterZ=0 NormalX=0 NormalY=0 NormalZ=1 AngleXU=0 Radius=138.257 StartAngle=2.51608 EndAngle=2.537
    g213: ArcOfCircle CenterX=522.868 CenterY=911.412 CenterZ=0 NormalX=0 NormalY=0 NormalZ=1 AngleXU=0 Radius=178.081 StartAngle=2.537 EndAngle=2.5543
    g214: ArcOfCircle CenterX=509.271 CenterY=920.462 CenterZ=0 NormalX=0 NormalY=0 NormalZ=1 AngleXU=0 Radius=161.747 StartAngle=2.5543 EndAngle=2.57178
    g215: ArcOfCircle CenterX=409.373 CenterY=984.468 CenterZ=0 NormalX=0 NormalY=0 NormalZ=1 AngleXU=0 Radius=43.1033 StartAngle=2.57178 EndAngle=2.61851
    g216: ArcOfCircle CenterX=290.86 CenterY=1052.81 CenterZ=0 NormalX=0 NormalY=0 NormalZ=1 AngleXU=-3.14159 Radius=93.7027 StartAngle=2.59608 EndAngle=2.61851
    g217: ArcOfCircle CenterX=-29.5136 CenterY=1247.26 CenterZ=0 NormalX=0 NormalY=0 NormalZ=1 AngleXU=-3.14159 Radius=468.469 StartAngle=2.58928 EndAngle=2.59608
    g218: ArcOfCircle CenterX=-29.0768 CenterY=1246.54 CenterZ=0 NormalX=0 NormalY=0 NormalZ=1 AngleXU=-3.14159 Radius=467.717 StartAngle=2.57504 EndAngle=2.58246
    g219: ArcOfCircle CenterX=474.955 CenterY=925.914 CenterZ=0 NormalX=0 NormalY=0 NormalZ=1 AngleXU=0 Radius=129.649 StartAngle=2.57504 EndAngle=2.63054
    g220: ArcOfCircle CenterX=537.375 CenterY=890.912 CenterZ=0 NormalX=0 NormalY=0 NormalZ=1 AngleXU=0 Radius=201.213 StartAngle=2.63054 EndAngle=2.67046
    g221: ArcOfCircle CenterX=535.022 CenterY=892.111 CenterZ=0 NormalX=0 NormalY=0 NormalZ=1 AngleXU=0 Radius=198.572 StartAngle=2.67046 EndAngle=2.71057
    g222: ArcOfCircle CenterX=461.325 CenterY=926.001 CenterZ=0 NormalX=0 NormalY=0 NormalZ=1 AngleXU=0 Radius=117.457 StartAngle=2.71057 EndAngle=2.77
    g223: ArcOfCircle CenterX=190.729 CenterY=1031.45 CenterZ=0 NormalX=0 NormalY=0 NormalZ=1 AngleXU=-3.14159 Radius=172.96 StartAngle=2.75475 EndAngle=2.77001
    g224: ArcOfCircle CenterX=-77.2056 CenterY=1276.65 CenterZ=0 NormalX=0 NormalY=0 NormalZ=1 AngleXU=-3.14159 Radius=524.491 StartAngle=2.58246 EndAngle=2.58928
    g225: ArcOfCircle CenterX=-124.997 CenterY=1160.29 CenterZ=0 NormalX=0 NormalY=0 NormalZ=1 AngleXU=-3.14159 Radius=513.962 StartAngle=2.74068 EndAngle=2.74768
    g226: ArcOfCircle CenterX=43.9966 CenterY=1088.66 CenterZ=0 NormalX=0 NormalY=0 NormalZ=1 AngleXU=-3.14159 Radius=330.414 StartAngle=2.73093 EndAngle=2.74068
    g227: ArcOfCircle CenterX=1431.14 CenterY=484.668 CenterZ=0 NormalX=0 NormalY=0 NormalZ=1 AngleXU=0 Radius=1182.52 StartAngle=2.73093 EndAngle=2.7338
    g228: ArcOfCircle CenterX=2719.33 CenterY=-71.8458 CenterZ=0 NormalX=0 NormalY=0 NormalZ=1 AngleXU=0 Radius=2585.78 StartAngle=2.7338 EndAngle=2.73539
    g229: ArcOfCircle CenterX=2753.56 CenterY=-86.5755 CenterZ=0 NormalX=0 NormalY=0 NormalZ=1 AngleXU=0 Radius=2623.05 StartAngle=2.73539 EndAngle=2.73698
    g230: ArcOfCircle CenterX=1609.36 CenterY=403.415 CenterZ=0 NormalX=0 NormalY=0 NormalZ=1 AngleXU=0 Radius=1378.35 StartAngle=2.73698 EndAngle=2.73956
    g231: ArcOfCircle CenterX=-845.736 CenterY=1447.31 CenterZ=0 NormalX=0 NormalY=0 NormalZ=1 AngleXU=-3.14159 Radius=1289.47 StartAngle=2.73709 EndAngle=2.73956
    g232: ArcOfCircle CenterX=-97.8292 CenterY=1149 CenterZ=0 NormalX=0 NormalY=0 NormalZ=1 AngleXU=-3.14159 Radius=484.542 StartAngle=2.74768 EndAngle=2.75476
    g233: ArcOfCircle CenterX=-589.085 CenterY=1337.25 CenterZ=0 NormalX=0 NormalY=0 NormalZ=1 AngleXU=-3.14159 Radius=1010.21 StartAngle=2.73171 EndAngle=2.73426
    g234: ArcOfCircle CenterX=265.324 CenterY=966.022 CenterZ=0 NormalX=0 NormalY=0 NormalZ=1 AngleXU=-3.14159 Radius=78.6418 StartAngle=2.71524 EndAngle=2.73172
    g235: ArcOfCircle CenterX=362.247 CenterY=921.999 CenterZ=0 NormalX=0 NormalY=0 NormalZ=1 AngleXU=0 Radius=27.8097 StartAngle=2.71524 EndAngle=2.85256
    g236: ArcOfCircle CenterX=1748.11 CenterY=509.898 CenterZ=0 NormalX=0 NormalY=0 NormalZ=1 AngleXU=0 Radius=1473.65 StartAngle=2.85256 EndAngle=2.86049
    g237: ArcOfCircle CenterX=408.58 CenterY=885.733 CenterZ=0 NormalX=0 NormalY=0 NormalZ=1 AngleXU=0 Radius=82.3714 StartAngle=2.87181 EndAngle=2.94281
    g238: ArcOfCircle CenterX=1304.21 CenterY=638.07 CenterZ=0 NormalX=0 NormalY=0 NormalZ=1 AngleXU=0 Radius=1011.62 StartAngle=2.8605 EndAngle=2.87181
    g239: ArcOfCircle CenterX=276.281 CenterY=912.384 CenterZ=0 NormalX=0 NormalY=0 NormalZ=1 AngleXU=-3.14159 Radius=52.5852 StartAngle=2.89856 EndAngle=2.94281
    g240: ArcOfCircle CenterX=113.397 CenterY=952.768 CenterZ=0 NormalX=0 NormalY=0 NormalZ=1 AngleXU=-3.14159 Radius=220.4 StartAngle=2.8833 EndAngle=2.89856
    g241: ArcOfCircle CenterX=-643.098 CenterY=1360.56 CenterZ=0 NormalX=0 NormalY=0 NormalZ=1 AngleXU=-3.14159 Radius=1069.04 StartAngle=2.73426 EndAngle=2.73709
    g242: ArcOfCircle CenterX=89.7922 CenterY=959.004 CenterZ=0 NormalX=0 NormalY=0 NormalZ=1 AngleXU=-3.14159 Radius=244.816 StartAngle=2.86815 EndAngle=2.8833
    g243: ArcOfCircle CenterX=131.591 CenterY=947.281 CenterZ=0 NormalX=0 NormalY=0 NormalZ=1 AngleXU=-3.14159 Radius=201.403 StartAngle=2.85061 EndAngle=2.86815
    g244: ArcOfCircle CenterX=484.317 CenterY=841.646 CenterZ=0 NormalX=0 NormalY=0 NormalZ=1 AngleXU=0 Radius=166.8 StartAngle=2.85061 EndAngle=2.87375
    g245: ArcOfCircle CenterX=687.516 CenterY=785.882 CenterZ=0 NormalX=0 NormalY=0 NormalZ=1 AngleXU=0 Radius=377.512 StartAngle=2.87375 EndAngle=2.88632
    g246: ArcOfCircle CenterX=695.357 CenterY=783.835 CenterZ=0 NormalX=0 NormalY=0 NormalZ=1 AngleXU=0 Radius=385.616 StartAngle=2.88632 EndAngle=2.89884
    g247: ArcOfCircle CenterX=524.004 CenterY=826.268 CenterZ=0 NormalX=0 NormalY=0 NormalZ=1 AngleXU=0 Radius=209.087 StartAngle=2.89884 EndAngle=2.91864
    g248: ArcOfCircle CenterX=483.207 CenterY=835.518 CenterZ=0 NormalX=0 NormalY=0 NormalZ=1 AngleXU=0 Radius=167.255 StartAngle=2.91864 EndAngle=2.95678
    g249: ArcOfCircle CenterX=485.251 CenterY=835.136 CenterZ=0 NormalX=0 NormalY=0 NormalZ=1 AngleXU=0 Radius=169.334 StartAngle=2.95679 EndAngle=2.99458
    g250: ArcOfCircle CenterX=655.033 CenterY=809.995 CenterZ=0 NormalX=0 NormalY=0 NormalZ=1 AngleXU=0 Radius=340.967 StartAngle=2.99458 EndAngle=3.01922
    g251: ArcOfCircle CenterX=2524.9 CenterY=580.019 CenterZ=0 NormalX=0 NormalY=0 NormalZ=1 AngleXU=0 Radius=2224.92 StartAngle=3.01922 EndAngle=3.02538
    g252: ArcOfCircle CenterX=420.182 CenterY=825.719 CenterZ=0 NormalX=0 NormalY=0 NormalZ=1 AngleXU=0 Radius=105.913 StartAngle=3.02538 EndAngle=3.10929
    g253: ArcOfCircle CenterX=687.806 CenterY=817.071 CenterZ=0 NormalX=0 NormalY=0 NormalZ=1 AngleXU=0 Radius=373.676 StartAngle=3.10929 EndAngle=3.14211
    g254: ArcOfCircle CenterX=690.089 CenterY=817.072 CenterZ=0 NormalX=0 NormalY=0 NormalZ=1 AngleXU=0 Radius=375.96 StartAngle=3.14212 EndAngle=3.1744
    g255: ArcOfCircle CenterX=399.132 CenterY=807.524 CenterZ=0 NormalX=0 NormalY=0 NormalZ=1 AngleXU=0 Radius=84.8463 StartAngle=3.1744 EndAngle=3.27188
    g256: ArcOfCircle CenterX=936.715 CenterY=877.966 CenterZ=0 NormalX=0 NormalY=0 NormalZ=1 AngleXU=0 Radius=627.025 StartAngle=3.27189 EndAngle=3.28701
    g257: ArcOfCircle CenterX=1845.8 CenterY=1011.1 CenterZ=0 NormalX=0 NormalY=0 NormalZ=1 AngleXU=0 Radius=1545.81 StartAngle=3.28701 EndAngle=3.29472
    g258: ArcOfCircle CenterX=1916.23 CenterY=1021.97 CenterZ=0 NormalX=0 NormalY=0 NormalZ=1 AngleXU=0 Radius=1617.07 StartAngle=3.29472 EndAngle=3.30174
    g259: ArcOfCircle CenterX=533.676 CenterY=798.639 CenterZ=0 NormalX=0 NormalY=0 NormalZ=1 AngleXU=0 Radius=216.595 StartAngle=3.30174 EndAngle=3.33269
    g260: ArcOfCircle CenterX=406.738 CenterY=774.082 CenterZ=0 NormalX=0 NormalY=0 NormalZ=1 AngleXU=0 Radius=87.3033 StartAngle=3.33269 EndAngle=3.42069
    g261: ArcOfCircle CenterX=1006.93 CenterY=946.086 CenterZ=0 NormalX=0 NormalY=0 NormalZ=1 AngleXU=0 Radius=711.66 StartAngle=3.42069 EndAngle=3.43946
    g262: ArcOfCircle CenterX=1063.27 CenterY=963.38 CenterZ=0 NormalX=0 NormalY=0 NormalZ=1 AngleXU=0 Radius=770.587 StartAngle=3.43946 EndAngle=3.45676
    g263: ArcOfCircle CenterX=387.682 CenterY=743.119 CenterZ=0 NormalX=0 NormalY=0 NormalZ=1 AngleXU=0 Radius=60.0029 StartAngle=3.45676 EndAngle=3.56875
    g264: ArcOfCircle CenterX=303.543 CenterY=704.82 CenterZ=0 NormalX=0 NormalY=0 NormalZ=1 AngleXU=-3.14159 Radius=32.4424 StartAngle=3.50997 EndAngle=3.56875
    g265: ArcOfCircle CenterX=305.025 CenterY=705.393 CenterZ=0 NormalX=0 NormalY=0 NormalZ=1 AngleXU=-3.14159 Radius=30.8537 StartAngle=3.44893 EndAngle=3.50996
    g266: ArcOfCircle CenterX=308.773 CenterY=706.582 CenterZ=0 NormalX=0 NormalY=0 NormalZ=1 AngleXU=-3.14159 Radius=26.9211 StartAngle=3.38844 EndAngle=3.44892
    g267: ArcOfCircle CenterX=330.993 CenterY=712.181 CenterZ=0 NormalX=0 NormalY=0 NormalZ=1 AngleXU=-3.14159 Radius=4.00743 StartAngle=3.14159 EndAngle=3.38844
    g268: ArcOfCircle CenterX=345.235 CenterY=712.181 CenterZ=0 NormalX=0 NormalY=0 NormalZ=1 AngleXU=0 Radius=10.2351 StartAngle=3.14159 EndAngle=3.45575
    g269: ArcOfCircle CenterX=651.396 CenterY=811.659 CenterZ=0 NormalX=0 NormalY=0 NormalZ=1 AngleXU=0 Radius=332.152 StartAngle=3.45575 EndAngle=3.48118
    g270: ArcOfCircle CenterX=593.896 CenterY=791.387 CenterZ=0 NormalX=0 NormalY=0 NormalZ=1 AngleXU=0 Radius=271.184 StartAngle=3.51689 EndAngle=3.55249
    g271: ArcOfCircle CenterX=592.916 CenterY=791 CenterZ=0 NormalX=0 NormalY=0 NormalZ=1 AngleXU=0 Radius=270.13 StartAngle=3.48118 EndAngle=3.51689
    g272: ArcOfCircle CenterX=1060.44 CenterY=560.892 CenterZ=0 NormalX=0 NormalY=0 NormalZ=1 AngleXU=0 Radius=0.559864 StartAngle=5.63029 EndAngle=6.28319
    g273: ArcOfCircle CenterX=383.064 CenterY=699.527 CenterZ=0 NormalX=0 NormalY=0 NormalZ=1 AngleXU=0 Radius=41.209 StartAngle=3.55249 EndAngle=3.69329
    g274: ArcOfCircle CenterX=635.377 CenterY=854.81 CenterZ=0 NormalX=0 NormalY=0 NormalZ=1 AngleXU=0 Radius=337.476 StartAngle=3.69329 EndAngle=3.72321
    g275: ArcOfCircle CenterX=632.895 CenterY=853.178 CenterZ=0 NormalX=0 NormalY=0 NormalZ=1 AngleXU=0 Radius=334.507 StartAngle=3.72321 EndAngle=3.75343
    g276: ArcOfCircle CenterX=394.681 CenterY=686.032 CenterZ=0 NormalX=0 NormalY=0 NormalZ=1 AngleXU=0 Radius=43.5013 StartAngle=3.75343 EndAngle=3.88934
    g277: ArcOfCircle CenterX=378.649 CenterY=671.164 CenterZ=0 NormalX=0 NormalY=0 NormalZ=1 AngleXU=0 Radius=21.636 StartAngle=3.88934 EndAngle=3.97708
    g278: ArcOfCircle CenterX=394.704 CenterY=688.914 CenterZ=0 NormalX=0 NormalY=0 NormalZ=1 AngleXU=0 Radius=45.5702 StartAngle=3.97707 EndAngle=4.02734
    g279: ArcOfCircle CenterX=395.022 CenterY=689.303 CenterZ=0 NormalX=0 NormalY=0 NormalZ=1 AngleXU=0 Radius=46.0731 StartAngle=4.02734 EndAngle=4.07748
    g280: ArcOfCircle CenterX=382.013 CenterY=671.644 CenterZ=0 NormalX=0 NormalY=0 NormalZ=1 AngleXU=0 Radius=24.1398 StartAngle=4.07748 EndAngle=4.15881
    g281: ArcOfCircle CenterX=359.09 CenterY=634.554 CenterZ=0 NormalX=0 NormalY=0 NormalZ=1 AngleXU=-3.14159 Radius=19.4628 StartAngle=4.04105 EndAngle=4.15882
    g282: ArcOfCircle CenterX=305.392 CenterY=566.961 CenterZ=0 NormalX=0 NormalY=0 NormalZ=1 AngleXU=-3.14159 Radius=105.789 StartAngle=4.00743 EndAngle=4.04105
    g283: ArcOfCircle CenterX=296.63 CenterY=556.662 CenterZ=0 NormalX=0 NormalY=0 NormalZ=1 AngleXU=-3.14159 Radius=119.311 StartAngle=3.9737 EndAngle=4.00743
    g284: ArcOfCircle CenterX=301.66 CenterY=562.186 CenterZ=0 NormalX=0 NormalY=0 NormalZ=1 AngleXU=-3.14159 Radius=111.84 StartAngle=3.9383 EndAngle=3.9737
    g285: ArcOfCircle CenterX=623.991 CenterY=891.892 CenterZ=0 NormalX=0 NormalY=0 NormalZ=1 AngleXU=0 Radius=349.249 StartAngle=3.9383 EndAngle=3.94983
    g286: ArcOfCircle CenterX=674.367 CenterY=944.624 CenterZ=0 NormalX=0 NormalY=0 NormalZ=1 AngleXU=0 Radius=422.177 StartAngle=3.94983 EndAngle=3.95983
    g287: ArcOfCircle CenterX=645.469 CenterY=913.763 CenterZ=0 NormalX=0 NormalY=0 NormalZ=1 AngleXU=0 Radius=379.897 StartAngle=3.95983 EndAngle=3.96989
    g288: ArcOfCircle CenterX=449.031 CenterY=699.702 CenterZ=0 NormalX=0 NormalY=0 NormalZ=1 AngleXU=0 Radius=89.3636 StartAngle=3.96989 EndAngle=3.99938
    g289: ArcOfCircle CenterX=251.367 CenterY=471.129 CenterZ=0 NormalX=0 NormalY=0 NormalZ=1 AngleXU=-3.14159 Radius=212.822 StartAngle=3.98653 EndAngle=3.99938
    g290: ArcOfCircle CenterX=-476.034 CenterY=-347.718 CenterZ=0 NormalX=0 NormalY=0 NormalZ=1 AngleXU=-3.14159 Radius=1308.1 StartAngle=3.97922 EndAngle=3.98289
    g291: ArcOfCircle CenterX=-412.824 CenterY=-277.534 CenterZ=0 NormalX=0 NormalY=0 NormalZ=1 AngleXU=-3.14159 Radius=1213.64 StartAngle=3.97533 EndAngle=3.97922
    g292: ArcOfCircle CenterX=592.435 CenterY=829.934 CenterZ=0 NormalX=0 NormalY=0 NormalZ=1 AngleXU=0 Radius=282.026 StartAngle=3.97533 EndAngle=3.99099
    g293: ArcOfCircle CenterX=519.463 CenterY=746.969 CenterZ=0 NormalX=0 NormalY=0 NormalZ=1 AngleXU=0 Radius=171.537 StartAngle=3.99099 EndAngle=4.01371
    g294: ArcOfCircle CenterX=583.636 CenterY=823.362 CenterZ=0 NormalX=0 NormalY=0 NormalZ=1 AngleXU=0 Radius=271.307 StartAngle=4.01371 EndAngle=4.02583
    g295: ArcOfCircle CenterX=413.098 CenterY=615.279 CenterZ=0 NormalX=0 NormalY=0 NormalZ=1 AngleXU=0 Radius=2.26813 StartAngle=4.02583 EndAngle=4.3908
    g296: ArcOfCircle CenterX=411.627 CenterY=610.864 CenterZ=0 NormalX=0 NormalY=0 NormalZ=1 AngleXU=-3.14159 Radius=2.38517 StartAngle=4.10525 EndAngle=4.3908
    g297: ArcOfCircle CenterX=-382.071 CenterY=-242.616 CenterZ=0 NormalX=0 NormalY=0 NormalZ=1 AngleXU=-3.14159 Radius=1167.12 StartAngle=3.98289 EndAngle=3.98653
    g298: ArcOfCircle CenterX=395.277 CenterY=587.547 CenterZ=0 NormalX=0 NormalY=0 NormalZ=1 AngleXU=-3.14159 Radius=30.8662 StartAngle=4.00781 EndAngle=4.05848
    g299: ArcOfCircle CenterX=390.741 CenterY=582.212 CenterZ=0 NormalX=0 NormalY=0 NormalZ=1 AngleXU=-3.14159 Radius=37.8687 StartAngle=3.96434 EndAngle=4.00781
    g300: ArcOfCircle CenterX=435.791 CenterY=630.759 CenterZ=0 NormalX=0 NormalY=0 NormalZ=1 AngleXU=0 Radius=28.3597 StartAngle=3.96434 EndAngle=4.09401
    g301: ArcOfCircle CenterX=467.91 CenterY=675.904 CenterZ=0 NormalX=0 NormalY=0 NormalZ=1 AngleXU=0 Radius=83.7646 StartAngle=4.09401 EndAngle=4.15184
    g302: ArcOfCircle CenterX=468.425 CenterY=676.725 CenterZ=0 NormalX=0 NormalY=0 NormalZ=1 AngleXU=0 Radius=84.7343 StartAngle=4.15184 EndAngle=4.20746
    g303: ArcOfCircle CenterX=435.319 CenterY=616.828 CenterZ=0 NormalX=0 NormalY=0 NormalZ=1 AngleXU=0 Radius=16.2971 StartAngle=4.20746 EndAngle=4.39612
    g304: ArcOfCircle CenterX=428.762 CenterY=596.794 CenterZ=0 NormalX=0 NormalY=0 NormalZ=1 AngleXU=-3.14159 Radius=4.78298 StartAngle=4.24444 EndAngle=4.39611
    g305: ArcOfCircle CenterX=429.341 CenterY=597.94 CenterZ=0 NormalX=0 NormalY=0 NormalZ=1 AngleXU=-3.14159 Radius=3.49903 StartAngle=4.05271 EndAngle=4.24443
    g306: ArcOfCircle CenterX=396.91 CenterY=589.679 CenterZ=0 NormalX=0 NormalY=0 NormalZ=1 AngleXU=-3.14159 Radius=28.181 StartAngle=4.05848 EndAngle=4.10526
    g307: ArcOfCircle CenterX=429.983 CenterY=598.766 CenterZ=0 NormalX=0 NormalY=0 NormalZ=1 AngleXU=-3.14159 Radius=2.45266 StartAngle=3.82948 EndAngle=4.05271
    g308: ArcOfCircle CenterX=431.462 CenterY=599.982 CenterZ=0 NormalX=0 NormalY=0 NormalZ=1 AngleXU=-3.14159 Radius=0.537881 StartAngle=3.14159 EndAngle=3.82948
    g309: ArcOfCircle CenterX=433.139 CenterY=599.982 CenterZ=0 NormalX=0 NormalY=0 NormalZ=1 AngleXU=0 Radius=1.13923 StartAngle=3.14159 EndAngle=4.12669
    g310: ArcOfCircle CenterX=463.819 CenterY=646.232 CenterZ=0 NormalX=0 NormalY=0 NormalZ=1 AngleXU=0 Radius=56.6399 StartAngle=4.1267 EndAngle=4.18627
    g311: ArcOfCircle CenterX=460.149 CenterY=639.914 CenterZ=0 NormalX=0 NormalY=0 NormalZ=1 AngleXU=0 Radius=49.3329 StartAngle=4.18627 EndAngle=4.26832
    g312: ArcOfCircle CenterX=467.334 CenterY=655.015 CenterZ=0 NormalX=0 NormalY=0 NormalZ=1 AngleXU=0 Radius=66.0561 StartAngle=4.26831 EndAngle=4.33424
    g313: ArcOfCircle CenterX=424.987 CenterY=548.42 CenterZ=0 NormalX=0 NormalY=0 NormalZ=1 AngleXU=-3.14159 Radius=48.642 StartAngle=4.22948 EndAngle=4.33424
    g314: ArcOfCircle CenterX=349.96 CenterY=405.326 CenterZ=0 NormalX=0 NormalY=0 NormalZ=1 AngleXU=-3.14159 Radius=210.212 StartAngle=4.19414 EndAngle=4.22947
    g315: ArcOfCircle CenterX=298.914 CenterY=315.81 CenterZ=0 NormalX=0 NormalY=0 NormalZ=1 AngleXU=-3.14159 Radius=313.26 StartAngle=4.17058 EndAngle=4.19414
    g316: ArcOfCircle CenterX=456.151 CenterY=577.047 CenterZ=0 NormalX=0 NormalY=0 NormalZ=1 AngleXU=-3.14159 Radius=8.35377 StartAngle=3.84897 EndAngle=4.17058
    g317: ArcOfCircle CenterX=468.794 CenterY=587.856 CenterZ=0 NormalX=0 NormalY=0 NormalZ=1 AngleXU=0 Radius=8.28062 StartAngle=3.84897 EndAngle=4.10602
    g318: ArcOfCircle CenterX=550.409 CenterY=705.536 CenterZ=0 NormalX=0 NormalY=0 NormalZ=1 AngleXU=0 Radius=151.492 StartAngle=4.10602 EndAngle=4.13698
    g319: ArcOfCircle CenterX=534.634 CenterY=681.216 CenterZ=0 NormalX=0 NormalY=0 NormalZ=1 AngleXU=0 Radius=122.504 StartAngle=4.13698 EndAngle=4.177
    g320: ArcOfCircle CenterX=495.539 CenterY=615.308 CenterZ=0 NormalX=0 NormalY=0 NormalZ=1 AngleXU=0 Radius=45.8728 StartAngle=4.177 EndAngle=4.26031
    g321: ArcOfCircle CenterX=460.538 CenterY=543.233 CenterZ=0 NormalX=0 NormalY=0 NormalZ=1 AngleXU=-3.14159 Radius=34.2506 StartAngle=4.21903 EndAngle=4.26031
    g322: ArcOfCircle CenterX=456.671 CenterY=536.041 CenterZ=0 NormalX=0 NormalY=0 NormalZ=1 AngleXU=-3.14159 Radius=42.4171 StartAngle=4.18388 EndAngle=4.21904
    g323: ArcOfCircle CenterX=458.795 CenterY=539.679 CenterZ=0 NormalX=0 NormalY=0 NormalZ=1 AngleXU=-3.14159 Radius=38.204 StartAngle=4.14833 EndAngle=4.18387
    g324: ArcOfCircle CenterX=474.048 CenterY=563.79 CenterZ=0 NormalX=0 NormalY=0 NormalZ=1 AngleXU=-3.14159 Radius=9.67346 StartAngle=4.04964 EndAngle=4.14833
    g325: ArcOfCircle CenterX=484.999 CenterY=577.82 CenterZ=0 NormalX=0 NormalY=0 NormalZ=1 AngleXU=0 Radius=8.12425 StartAngle=4.04964 EndAngle=4.19775
    g326: ArcOfCircle CenterX=581.968 CenterY=749.307 CenterZ=0 NormalX=0 NormalY=0 NormalZ=1 AngleXU=0 Radius=205.129 StartAngle=4.19775 EndAngle=4.21201
    g327: ArcOfCircle CenterX=576.202 CenterY=738.761 CenterZ=0 NormalX=0 NormalY=0 NormalZ=1 AngleXU=0 Radius=193.11 StartAngle=4.21201 EndAngle=4.23009
    g328: ArcOfCircle CenterX=610.059 CenterY=803.43 CenterZ=0 NormalX=0 NormalY=0 NormalZ=1 AngleXU=0 Radius=266.105 StartAngle=4.23009 EndAngle=4.24431
    g329: ArcOfCircle CenterX=389.085 CenterY=366.331 CenterZ=0 NormalX=0 NormalY=0 NormalZ=1 AngleXU=-3.14159 Radius=223.675 StartAngle=4.22645 EndAngle=4.24431
    g330: ArcOfCircle CenterX=387.489 CenterY=362.372 CenterZ=0 NormalX=0 NormalY=0 NormalZ=1 AngleXU=-3.14159 Radius=227.918 StartAngle=4.19405 EndAngle=4.21026
    g331: ArcOfCircle CenterX=476.822 CenterY=518.999 CenterZ=0 NormalX=0 NormalY=0 NormalZ=1 AngleXU=-3.14159 Radius=47.6061 StartAngle=4.14226 EndAngle=4.19405
    g332: ArcOfCircle CenterX=1223.6 CenterY=1683.75 CenterZ=0 NormalX=0 NormalY=0 NormalZ=1 AngleXU=0 Radius=1335.99 StartAngle=4.14226 EndAngle=4.14649
    g333: ArcOfCircle CenterX=550.224 CenterY=623.646 CenterZ=0 NormalX=0 NormalY=0 NormalZ=1 AngleXU=0 Radius=80.0959 StartAngle=4.14648 EndAngle=4.17938
    g334: ArcOfCircle CenterX=523.451 CenterY=578.265 CenterZ=0 NormalX=0 NormalY=0 NormalZ=1 AngleXU=0 Radius=27.406 StartAngle=4.17938 EndAngle=4.24571
    g335: ArcOfCircle CenterX=525.228 CenterY=581.793 CenterZ=0 NormalX=0 NormalY=0 NormalZ=1 AngleXU=0 Radius=31.356 StartAngle=4.24571 EndAngle=4.30567
    g336: ArcOfCircle CenterX=492.658 CenterY=506.179 CenterZ=0 NormalX=0 NormalY=0 NormalZ=1 AngleXU=-3.14159 Radius=50.9737 StartAngle=4.27564 EndAngle=4.30567
    g337: ArcOfCircle CenterX=166.986 CenterY=-191.473 CenterZ=0 NormalX=0 NormalY=0 NormalZ=1 AngleXU=-3.14159 Radius=820.897 StartAngle=4.27169 EndAngle=4.27564
    g338: ArcOfCircle CenterX=374.46 CenterY=338.643 CenterZ=0 NormalX=0 NormalY=0 NormalZ=1 AngleXU=-3.14159 Radius=254.988 StartAngle=4.21027 EndAngle=4.22645
    g339: ArcOfCircle CenterX=159.38 CenterY=-207.602 CenterZ=0 NormalX=0 NormalY=0 NormalZ=1 AngleXU=-3.14159 Radius=838.729 StartAngle=4.2671 EndAngle=4.27169
    g340: ArcOfCircle CenterX=63.3224 CenterY=-408.872 CenterZ=0 NormalX=0 NormalY=0 NormalZ=1 AngleXU=-3.14159 Radius=1061.75 StartAngle=4.26325 EndAngle=4.2671
    g341: ArcOfCircle CenterX=648.363 CenterY=804.916 CenterZ=0 NormalX=0 NormalY=0 NormalZ=1 AngleXU=0 Radius=285.679 StartAngle=4.26325 EndAngle=4.27841
    g342: ArcOfCircle CenterX=680.143 CenterY=873.491 CenterZ=0 NormalX=0 NormalY=0 NormalZ=1 AngleXU=0 Radius=361.26 StartAngle=4.27841 EndAngle=4.29113
    g343: ArcOfCircle CenterX=666.188 CenterY=842.347 CenterZ=0 NormalX=0 NormalY=0 NormalZ=1 AngleXU=0 Radius=327.132 StartAngle=4.29113 EndAngle=4.30396
    g344: ArcOfCircle CenterX=569.616 CenterY=619.196 CenterZ=0 NormalX=0 NormalY=0 NormalZ=1 AngleXU=0 Radius=83.981 StartAngle=4.30396 EndAngle=4.33923
    g345: ArcOfCircle CenterX=490.387 CenterY=416.826 CenterZ=0 NormalX=0 NormalY=0 NormalZ=1 AngleXU=-3.14159 Radius=133.345 StartAngle=4.3187 EndAngle=4.33922
    g346: ArcOfCircle CenterX=423.987 CenterY=256.969 CenterZ=0 NormalX=0 NormalY=0 NormalZ=1 AngleXU=-3.14159 Radius=306.444 StartAngle=4.30768 EndAngle=4.3187
    g347: ArcOfCircle CenterX=478.144 CenterY=379.458 CenterZ=0 NormalX=0 NormalY=0 NormalZ=1 AngleXU=-3.14159 Radius=172.518 StartAngle=4.27954 EndAngle=4.29671
    g348: ArcOfCircle CenterX=614.754 CenterY=675.1 CenterZ=0 NormalX=0 NormalY=0 NormalZ=1 AngleXU=0 Radius=153.161 StartAngle=4.27954 EndAngle=4.29732
    g349: ArcOfCircle CenterX=613.716 CenterY=672.744 CenterZ=0 NormalX=0 NormalY=0 NormalZ=1 AngleXU=0 Radius=150.586 StartAngle=4.29732 EndAngle=4.31534
    g350: ArcOfCircle CenterX=564.862 CenterY=551.014 CenterZ=0 NormalX=0 NormalY=0 NormalZ=1 AngleXU=0 Radius=19.4167 StartAngle=4.3329 EndAngle=4.40615
    g351: ArcOfCircle CenterX=607.479 CenterY=657.87 CenterZ=0 NormalX=0 NormalY=0 NormalZ=1 AngleXU=0 Radius=134.458 StartAngle=4.31534 EndAngle=4.3329
    g352: ArcOfCircle CenterX=610.781 CenterY=565.228 CenterZ=0 NormalX=0 NormalY=0 NormalZ=1 AngleXU=0 Radius=52.3449 StartAngle=4.23138 EndAngle=4.2815
    g353: ArcOfCircle CenterX=555.009 CenterY=519.849 CenterZ=0 NormalX=0 NormalY=0 NormalZ=1 AngleXU=-3.14159 Radius=13.2683 StartAngle=4.29715 EndAngle=4.40615
    g354: ArcOfCircle CenterX=518.129 CenterY=436.2 CenterZ=0 NormalX=0 NormalY=0 NormalZ=1 AngleXU=-3.14159 Radius=104.687 StartAngle=4.27335 EndAngle=4.29715
    g355: ArcOfCircle CenterX=420.985 CenterY=249.963 CenterZ=0 NormalX=0 NormalY=0 NormalZ=1 AngleXU=-3.14159 Radius=314.066 StartAngle=4.29671 EndAngle=4.30768
    g356: ArcOfCircle CenterX=509.561 CenterY=418.402 CenterZ=0 NormalX=0 NormalY=0 NormalZ=1 AngleXU=-3.14159 Radius=124.441 StartAngle=4.22506 EndAngle=4.24863
    g357: ArcOfCircle CenterX=609.519 CenterY=607.015 CenterZ=0 NormalX=0 NormalY=0 NormalZ=1 AngleXU=0 Radius=89.0215 StartAngle=4.22506 EndAngle=4.25686
    g358: ArcOfCircle CenterX=597.308 CenterY=582.089 CenterZ=0 NormalX=0 NormalY=0 NormalZ=1 AngleXU=0 Radius=61.2659 StartAngle=4.25685 EndAngle=4.29893
    g359: ArcOfCircle CenterX=599.219 CenterY=586.444 CenterZ=0 NormalX=0 NormalY=0 NormalZ=1 AngleXU=0 Radius=66.0212 StartAngle=4.29893 EndAngle=4.33138
    g360: ArcOfCircle CenterX=575.483 CenterY=527.19 CenterZ=0 NormalX=0 NormalY=0 NormalZ=1 AngleXU=0 Radius=2.19041 StartAngle=4.33138 EndAngle=4.71239
    g361: ArcOfCircle CenterX=575.483 CenterY=523.19 CenterZ=0 NormalX=0 NormalY=0 NormalZ=1 AngleXU=-3.14159 Radius=1.8098 StartAngle=4.27001 EndAngle=4.71239
    g362: ArcOfCircle CenterX=512.995 CenterY=425.268 CenterZ=0 NormalX=0 NormalY=0 NormalZ=1 AngleXU=-3.14159 Radius=116.764 StartAngle=4.24863 EndAngle=4.27335
    g363: ArcOfCircle CenterX=559.611 CenterY=489.762 CenterZ=0 NormalX=0 NormalY=0 NormalZ=1 AngleXU=-3.14159 Radius=38.8158 StartAngle=4.16442 EndAngle=4.2217
    g364: ArcOfCircle CenterX=551.403 CenterY=476.312 CenterZ=0 NormalX=0 NormalY=0 NormalZ=1 AngleXU=-3.14159 Radius=54.5724 StartAngle=4.12005 EndAngle=4.16442
    g365: ArcOfCircle CenterX=605.492 CenterY=556.689 CenterZ=0 NormalX=0 NormalY=0 NormalZ=1 AngleXU=0 Radius=42.3099 StartAngle=4.12005 EndAngle=4.182
    g366: ArcOfCircle CenterX=613.056 CenterY=569.587 CenterZ=0 NormalX=0 NormalY=0 NormalZ=1 AngleXU=0 Radius=57.2623 StartAngle=4.182 EndAngle=4.23138
    g367: ArcOfCircle CenterX=595.547 CenterY=532.088 CenterZ=0 NormalX=0 NormalY=0 NormalZ=1 AngleXU=0 Radius=15.8709 StartAngle=4.2815 EndAngle=4.40343
    g368: ArcOfCircle CenterX=584.498 CenterY=497.47 CenterZ=0 NormalX=0 NormalY=0 NormalZ=1 AngleXU=-3.14159 Radius=20.4672 StartAngle=4.31095 EndAngle=4.40343
    g369: ArcOfCircle CenterX=569.893 CenterY=463.065 CenterZ=0 NormalX=0 NormalY=0 NormalZ=1 AngleXU=-3.14159 Radius=57.8431 StartAngle=4.26835 EndAngle=4.31095
    g370: ArcOfCircle CenterX=559.934 CenterY=490.367 CenterZ=0 NormalX=0 NormalY=0 NormalZ=1 AngleXU=-3.14159 Radius=38.1297 StartAngle=4.22171 EndAngle=4.27001
    g371: ArcOfCircle CenterX=568.221 CenterY=459.55 CenterZ=0 NormalX=0 NormalY=0 NormalZ=1 AngleXU=-3.14159 Radius=61.7357 StartAngle=4.22626 EndAngle=4.26835
    g372: ArcOfCircle CenterX=577.994 CenterY=478.043 CenterZ=0 NormalX=0 NormalY=0 NormalZ=1 AngleXU=-3.14159 Radius=40.8194 StartAngle=4.16887 EndAngle=4.22626
    g373: ArcOfCircle CenterX=623.342 CenterY=553.095 CenterZ=0 NormalX=0 NormalY=0 NormalZ=1 AngleXU=0 Radius=46.8694 StartAngle=4.16886 EndAngle=4.30205
    g374: ArcOfCircle CenterX=639.719 CenterY=590.74 CenterZ=0 NormalX=0 NormalY=0 NormalZ=1 AngleXU=0 Radius=87.922 StartAngle=4.30205 EndAngle=4.38521
    g375: ArcOfCircle CenterX=646.551 CenterY=610.871 CenterZ=0 NormalX=0 NormalY=0 NormalZ=1 AngleXU=0 Radius=109.181 StartAngle=4.38521 EndAngle=4.46027
    g376: ArcOfCircle CenterX=657.297 CenterY=652.584 CenterZ=0 NormalX=0 NormalY=0 NormalZ=1 AngleXU=0 Radius=152.256 StartAngle=4.46027 EndAngle=4.51876
    g377: ArcOfCircle CenterX=606.595 CenterY=394.008 CenterZ=0 NormalX=0 NormalY=0 NormalZ=1 AngleXU=-3.14159 Radius=111.244 StartAngle=4.47361 EndAngle=4.51877
    g378: ArcOfCircle CenterX=566.711 CenterY=230.166 CenterZ=0 NormalX=0 NormalY=0 NormalZ=1 AngleXU=-3.14159 Radius=279.871 StartAngle=4.45094 EndAngle=4.47361
    g379: ArcOfCircle CenterX=563.611 CenterY=218.58 CenterZ=0 NormalX=0 NormalY=0 NormalZ=1 AngleXU=-3.14159 Radius=291.865 StartAngle=4.42844 EndAngle=4.45094
    g380: ArcOfCircle CenterX=596.668 CenterY=331.849 CenterZ=0 NormalX=0 NormalY=0 NormalZ=1 AngleXU=-3.14159 Radius=173.87 StartAngle=4.39527 EndAngle=4.42844
    g381: ArcOfCircle CenterX=735.861 CenterY=755.971 CenterZ=0 NormalX=0 NormalY=0 NormalZ=1 AngleXU=0 Radius=272.508 StartAngle=4.39527 EndAngle=4.41497
    g382: ArcOfCircle CenterX=734.919 CenterY=752.897 CenterZ=0 NormalX=0 NormalY=0 NormalZ=1 AngleXU=0 Radius=269.294 StartAngle=4.41497 EndAngle=4.43485
    g383: ArcOfCircle CenterX=726.957 CenterY=724.947 CenterZ=0 NormalX=0 NormalY=0 NormalZ=1 AngleXU=0 Radius=240.231 StartAngle=4.43485 EndAngle=4.45425
    g384: ArcOfCircle CenterX=674.637 CenterY=526.786 CenterZ=0 NormalX=0 NormalY=0 NormalZ=1 AngleXU=0 Radius=35.2796 StartAngle=4.45425 EndAngle=4.53424
    g385: ArcOfCircle CenterX=681.565 CenterY=504.915 CenterZ=0 NormalX=0 NormalY=0 NormalZ=1 AngleXU=0 Radius=15.3287 StartAngle=4.4646 EndAngle=4.6429
    g386: ArcOfCircle CenterX=647.205 CenterY=374.433 CenterZ=0 NormalX=0 NormalY=0 NormalZ=1 AngleXU=-3.14159 Radius=119.523 StartAngle=4.5149 EndAngle=4.53424
    g387: ArcOfCircle CenterX=629.698 CenterY=286.94 CenterZ=0 NormalX=0 NormalY=0 NormalZ=1 AngleXU=-3.14159 Radius=208.75 StartAngle=4.50215 EndAngle=4.5149
    g388: ArcOfCircle CenterX=631.124 CenterY=293.62 CenterZ=0 NormalX=0 NormalY=0 NormalZ=1 AngleXU=-3.14159 Radius=201.92 StartAngle=4.48933 EndAngle=4.50215
    g389: ArcOfCircle CenterX=657.258 CenterY=408.834 CenterZ=0 NormalX=0 NormalY=0 NormalZ=1 AngleXU=-3.14159 Radius=83.779 StartAngle=4.4646 EndAngle=4.48933
    g390: ArcOfCircle CenterX=692.788 CenterY=-1565.91 CenterZ=0 NormalX=0 NormalY=0 NormalZ=1 AngleXU=-3.14159 Radius=2054.81 StartAngle=4.70341 EndAngle=4.708
    g391: ArcOfCircle CenterX=701.261 CenterY=787.913 CenterZ=0 NormalX=0 NormalY=0 NormalZ=1 AngleXU=0 Radius=299.012 StartAngle=4.6429 EndAngle=4.66344
    g392: ArcOfCircle CenterX=701.182 CenterY=786.285 CenterZ=0 NormalX=0 NormalY=0 NormalZ=1 AngleXU=0 Radius=297.382 StartAngle=4.66344 EndAngle=4.68807
    g393: ArcOfCircle CenterX=703.535 CenterY=883.009 CenterZ=0 NormalX=0 NormalY=0 NormalZ=1 AngleXU=0 Radius=394.134 StartAngle=4.68807 EndAngle=4.708
    g394: ArcOfCircle CenterX=658.288 CenterY=-5406.75 CenterZ=0 NormalX=0 NormalY=0 NormalZ=1 AngleXU=-3.14159 Radius=5895.81 StartAngle=4.70132 EndAngle=4.70341
    g395: ArcOfCircle CenterX=654.103 CenterY=-5784.73 CenterZ=0 NormalX=0 NormalY=0 NormalZ=1 AngleXU=-3.14159 Radius=6273.81 StartAngle=4.69924 EndAngle=4.70132
    g396: ArcOfCircle CenterX=682.64 CenterY=-3613.87 CenterZ=0 NormalX=0 NormalY=0 NormalZ=1 AngleXU=-3.14159 Radius=4102.76 StartAngle=4.6964 EndAngle=4.69924
    g397: ArcOfCircle CenterX=770.873 CenterY=1902.21 CenterZ=0 NormalX=0 NormalY=0 NormalZ=1 AngleXU=0 Radius=1414.02 StartAngle=4.69639 EndAngle=4.70565
    g398: ArcOfCircle CenterX=762.969 CenterY=729.457 CenterZ=0 NormalX=0 NormalY=0 NormalZ=1 AngleXU=0 Radius=241.248 StartAngle=4.70565 EndAngle=4.73989
    g399: ArcOfCircle CenterX=765.494 CenterY=637.667 CenterZ=0 NormalX=0 NormalY=0 NormalZ=1 AngleXU=0 Radius=149.422 StartAngle=4.73989 EndAngle=4.77724
    ... +780 more geometry lines
FEATURE [Part::Part2DObjectPython] Clone2D  label="Sketch1180 (2D)"  # Draft 2D object (typed FeaturePython)
  Fuse = false
  Objects = -> [Sketch1180]
  Scale = (0.5,0.5,1)
FEATURE [Part::Part2DObjectPython] Clone2D001  label="Sketch1180 (2D) (2D)"  # Draft 2D object (typed FeaturePython)
  Fuse = false
  Objects = -> [Clone2D]
  Scale = (0.1,0.1,1)
FEATURE [Part::Part2DObjectPython] Clone2D002  label="Sketch1180 (2D) (2D) (2D)"  # Draft 2D object (typed FeaturePython)
  Fuse = false
  Objects = -> [Clone2D001]
  Scale = (1,1,1)
FEATURE [Sketcher::SketchObject] Sketch
  sketch-geometry (60):
    g0: LineSegment StartX=37.2928 StartY=58.9704 StartZ=0 EndX=33.3665 EndY=59.6299 EndZ=0
    g1: LineSegment StartX=33.3665 StartY=59.6299 StartZ=0 EndX=30.86 EndY=59.516 EndZ=0
    g2: LineSegment StartX=30.86 StartY=59.516 StartZ=0 EndX=27.1572 EndY=58.9463 EndZ=0
    g3: LineSegment StartX=27.1572 StartY=58.9463 StartZ=0 EndX=26.0179 EndY=58.4906 EndZ=0
    g4: LineSegment StartX=26.0179 StartY=58.4906 StartZ=0 EndX=23.9102 EndY=57.1234 EndZ=0
    g5: LineSegment StartX=23.9102 StartY=57.1234 StartZ=0 EndX=21.2328 EndY=54.6739 EndZ=0
    g6: LineSegment StartX=21.2328 StartY=54.6739 StartZ=0 EndX=18.8403 EndY=52.3384 EndZ=0
    g7: LineSegment StartX=18.8403 StartY=52.3384 StartZ=0 EndX=17.8719 EndY=50.9712 EndZ=0
    g8: LineSegment StartX=17.8719 StartY=50.9712 StartZ=0 EndX=16.7896 EndY=49.1483 EndZ=0
    g9: LineSegment StartX=16.7896 StartY=49.1483 StartZ=0 EndX=15.7642 EndY=46.7558 EndZ=0
    g10: LineSegment StartX=15.7642 StartY=46.7558 StartZ=0 EndX=15.0236 EndY=43.7366 EndZ=0
    g11: LineSegment StartX=15.0236 StartY=43.7366 StartZ=0 EndX=14.7958 EndY=41.7428 EndZ=0
    g12: LineSegment StartX=14.7958 StartY=41.7428 StartZ=0 EndX=14.7958 EndY=39.5781 EndZ=0
    g13: LineSegment StartX=14.7958 StartY=39.5781 StartZ=0 EndX=15.1376 EndY=37.7553 EndZ=0
    g14: LineSegment StartX=15.1376 StartY=37.7553 StartZ=0 EndX=15.8781 EndY=35.3057 EndZ=0
    g15: LineSegment StartX=15.8781 StartY=35.3057 StartZ=0 EndX=16.7896 EndY=33.0271 EndZ=0
    g16: LineSegment StartX=16.7896 StartY=33.0271 StartZ=0 EndX=17.5871 EndY=31.8878 EndZ=0
    g17: LineSegment StartX=17.5871 StartY=31.8878 StartZ=0 EndX=21.1189 EndY=29.0965 EndZ=0
    g18: LineSegment StartX=21.1189 StartY=29.0965 StartZ=0 EndX=25.6192 EndY=26.5901 EndZ=0
    g19: LineSegment StartX=25.6192 StartY=26.5901 StartZ=0 EndX=29.8346 EndY=24.5963 EndZ=0
    g20: LineSegment StartX=29.8346 StartY=24.5963 StartZ=0 EndX=34.107 EndY=23.5139 EndZ=0
    g21: LineSegment StartX=34.107 StartY=23.5139 StartZ=0 EndX=36.8413 EndY=23.5139 EndZ=0
    g22: LineSegment StartX=36.8413 StartY=23.5139 StartZ=0 EndX=42.253 EndY=23.7418 EndZ=0
    g23: LineSegment StartX=42.253 StartY=23.7418 StartZ=0 EndX=46.3545 EndY=24.4254 EndZ=0
    g24: LineSegment StartX=46.3545 StartY=24.4254 StartZ=0 EndX=51.1396 EndY=25.9065 EndZ=0
    g25: LineSegment StartX=51.1396 StartY=25.9065 StartZ=0 EndX=54.8424 EndY=28.0142 EndZ=0
    g26: LineSegment StartX=54.8424 StartY=28.0142 StartZ=0 EndX=57.6906 EndY=29.894 EndZ=0
    g27: LineSegment StartX=57.6906 StartY=29.894 StartZ=0 EndX=60.1401 EndY=33.312 EndZ=0
    g28: LineSegment StartX=60.1401 StartY=33.312 StartZ=0 EndX=61.8491 EndY=36.2742 EndZ=0
    g29: LineSegment StartX=61.8491 StartY=36.2742 StartZ=0 EndX=62.9314 EndY=40.6035 EndZ=0
    g30: LineSegment StartX=62.9314 StartY=40.6035 StartZ=0 EndX=62.4187 EndY=45.5025 EndZ=0
    g31: LineSegment StartX=62.4187 StartY=45.5025 StartZ=0 EndX=61.5643 EndY=48.8635 EndZ=0
    g32: LineSegment StartX=61.5643 StartY=48.8635 StartZ=0 EndX=59.7983 EndY=52.3384 EndZ=0
    g33: LineSegment StartX=59.7983 StartY=52.3384 StartZ=0 EndX=57.1779 EndY=55.0727 EndZ=0
    g34: LineSegment StartX=57.1779 StartY=55.0727 StartZ=0 EndX=55.1842 EndY=56.155 EndZ=0
    g35: LineSegment StartX=55.1842 StartY=56.155 StartZ=0 EndX=57.8615 EndY=57.4652 EndZ=0
    g36: LineSegment StartX=57.8615 StartY=57.4652 StartZ=0 EndX=60.0832 EndY=59.8008 EndZ=0
    g37: LineSegment StartX=60.0832 StartY=59.8008 StartZ=0 EndX=60.7098 EndY=62.0794 EndZ=0
    g38: LineSegment StartX=60.7098 StartY=62.0794 StartZ=0 EndX=61.3364 EndY=65.0986 EndZ=0
    g39: LineSegment StartX=61.3364 StartY=65.0986 StartZ=0 EndX=62.6466 EndY=67.4342 EndZ=0
    g40: LineSegment StartX=62.6466 StartY=67.4342 StartZ=0 EndX=64.8113 EndY=69.6558 EndZ=0
    g41: LineSegment StartX=64.8113 StartY=69.6558 StartZ=0 EndX=67.5456 EndY=71.7635 EndZ=0
    g42: LineSegment StartX=67.5456 StartY=71.7635 StartZ=0 EndX=68.3431 EndY=72.9028 EndZ=0
    g43: LineSegment StartX=68.3431 StartY=72.9028 StartZ=0 EndX=68.2292 EndY=73.7003 EndZ=0
    g44: LineSegment StartX=68.2292 StartY=73.7003 StartZ=0 EndX=67.3177 EndY=74.3839 EndZ=0
    g45: LineSegment StartX=67.3177 StartY=74.3839 StartZ=0 EndX=63.5011 EndY=73.8143 EndZ=0
    g46: LineSegment StartX=63.5011 StartY=73.8143 StartZ=0 EndX=59.2856 EndY=73.3586 EndZ=0
    g47: LineSegment StartX=59.2856 StartY=73.3586 StartZ=0 EndX=55.5829 EndY=73.3586 EndZ=0
    g48: LineSegment StartX=55.5829 StartY=73.3586 StartZ=0 EndX=53.4752 EndY=73.3586 EndZ=0
    g49: LineSegment StartX=53.4752 StartY=73.3586 StartZ=0 EndX=50.9118 EndY=73.7573 EndZ=0
    g50: LineSegment StartX=50.9118 StartY=73.7573 StartZ=0 EndX=48.804 EndY=74.0421 EndZ=0
    g51: LineSegment StartX=48.804 StartY=74.0421 StartZ=0 EndX=45.8418 EndY=74.0421 EndZ=0
    g52: LineSegment StartX=45.8418 StartY=74.0421 StartZ=0 EndX=42.1961 EndY=73.1307 EndZ=0
    g53: LineSegment StartX=42.1961 StartY=73.1307 StartZ=0 EndX=39.4048 EndY=71.9344 EndZ=0
    g54: LineSegment StartX=39.4048 StartY=71.9344 StartZ=0 EndX=36.9553 EndY=70.5103 EndZ=0
    g55: LineSegment StartX=36.9553 StartY=70.5103 StartZ=0 EndX=35.3602 EndY=68.5735 EndZ=0
    g56: LineSegment StartX=35.3602 StartY=68.5735 StartZ=0 EndX=34.7336 EndY=65.8391 EndZ=0
    g57: LineSegment StartX=34.7336 StartY=65.8391 StartZ=0 EndX=34.7336 EndY=63.2187 EndZ=0
    g58: LineSegment StartX=34.7336 StartY=63.2187 StartZ=0 EndX=36.8413 EndY=59.9717 EndZ=0
    g59: LineSegment StartX=36.8413 StartY=59.9717 StartZ=0 EndX=37.2928 EndY=58.9704 EndZ=0
  constraints (66):
    c: Coincident(g0,g1)
    c: Coincident(g1,g2)
    c: Coincident(g2,g3)
    c: Coincident(g3,g4)
    c: Coincident(g4,g5)
    c: Coincident(g5,g6)
    c: Coincident(g6,g7)
    c: Coincident(g7,g8)
    c: Coincident(g8,g9)
    c: Coincident(g9,g10)
    c: Coincident(g10,g11)
    c: Coincident(g11,g12)
    c: Vertical(g12)
    c: Coincident(g12,g13)
    c: Coincident(g13,g14)
    c: Coincident(g14,g15)
    c: Coincident(g15,g16)
    c: Coincident(g16,g17)
    c: Coincident(g17,g18)
    c: Coincident(g18,g19)
    c: Coincident(g19,g20)
    c: Coincident(g20,g21)
    c: Horizontal(g21)
    c: Coincident(g21,g22)
    c: Coincident(g22,g23)
    c: Coincident(g23,g24)
    c: Coincident(g24,g25)
    c: Coincident(g25,g26)
    c: Coincident(g26,g27)
    c: Coincident(g27,g28)
    c: Coincident(g28,g29)
    c: Coincident(g29,g30)
    c: Coincident(g30,g31)
    c: Coincident(g31,g32)
    c: Coincident(g32,g33)
    c: Coincident(g33,g34)
    c: Coincident(g34,g35)
    c: Coincident(g35,g36)
    c: Coincident(g36,g37)
    c: Coincident(g37,g38)
    c: Coincident(g38,g39)
    c: Coincident(g39,g40)
    c: Coincident(g40,g41)
    c: Coincident(g41,g42)
    c: Coincident(g42,g43)
    c: Coincident(g43,g44)
    c: Coincident(g44,g45)
    c: Coincident(g45,g46)
    c: Coincident(g46,g47)
    c: Horizontal(g47)
    c: Coincident(g47,g48)
    c: Horizontal(g48)
    c: Coincident(g48,g49)
    c: Coincident(g49,g50)
    c: Coincident(g50,g51)
    c: Horizontal(g51)
    c: Coincident(g51,g52)
    c: Coincident(g52,g53)
    c: Coincident(g53,g54)
    c: Coincident(g54,g55)
    c: Coincident(g55,g56)
    c: Coincident(g56,g57)
    c: Vertical(g57)
    c: Coincident(g57,g58)
    c: Coincident(g58,g59)
    c: Coincident(g59,g0)
FEATURE [Part::Extrusion] Extrude
  Base = -> Sketch
  Dir = (0,0,1)
  DirMode = 2
  FaceMakerClass = Part::FaceMakerBullseye
  LengthFwd = 25
  LengthRev = 0
  Solid = true
  Symmetric = false
FEATURE [Part::Extrusion] Extrude001
  Base = -> Clone2D002
  Dir = (0,0,1)
  DirMode = 2
  FaceMakerClass = Part::FaceMakerBullseye
  LengthFwd = 30
  LengthRev = 0
  Placement = pos=(0,0,-2) rot=(0,0,1;0rad)
  Solid = true
  Symmetric = false
FEATURE [Part::Cut] Cut
  Base = -> Extrude
  Tool = -> Extrude001
